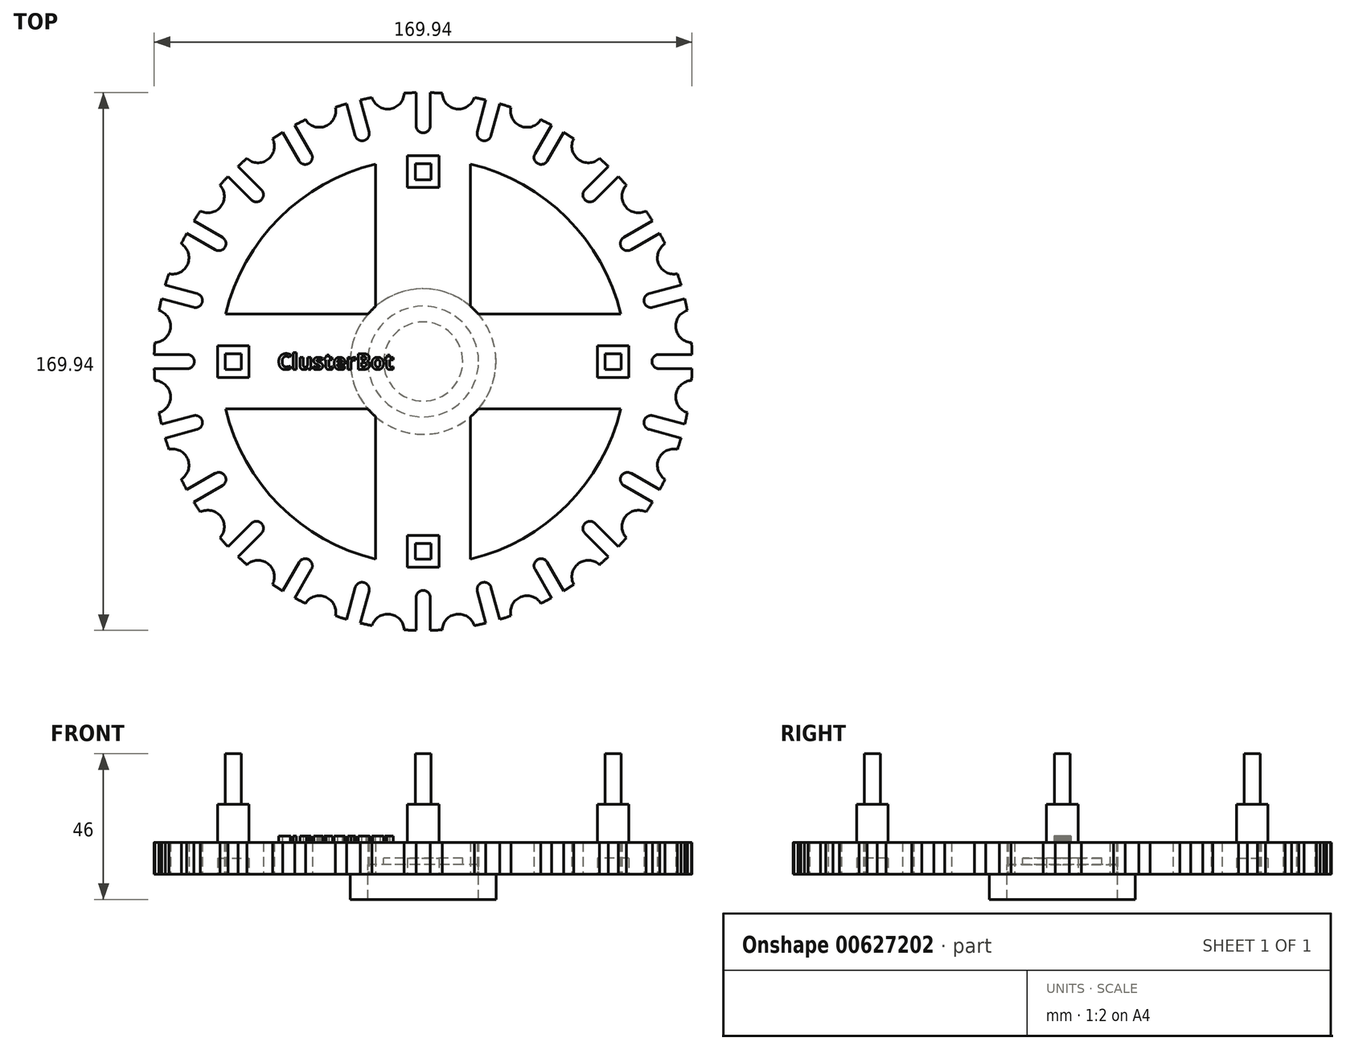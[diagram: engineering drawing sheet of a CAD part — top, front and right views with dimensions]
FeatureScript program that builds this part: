
annotation { "Feature Type Name" : "Feature", "Feature Type Description" : "" }
export const myFeature = defineFeature(function(context is Context, id is Id, definition is map)
    precondition{}
    {
        {
            var Q0;
            Q0=qCreatedBy(makeId("Top.planeOp"),FACE);
            var sketch = newSketch(context, id + "F0", { "sketchPlane" : qUnion([Q0])});
            skCircle(sketch, "E0", {"center": v(0, 0) * mm, "radius": 85 * mm});
            skLineSegment(sketch, "E1", {"start": v(0, 95.93) * mm, "end": v(0, -91) * mm, "construction": true});
            skLineSegment(sketch, "E2", {"start": v(-97.8, 0) * mm, "end": v(95.73, 0) * mm, "construction": true});
            skLineSegment(sketch, "E3", {"start": v(0, 85) * mm, "end": v(2.25, 85) * mm});
            skLineSegment(sketch, "E4", {"start": v(2.25, 85) * mm, "end": v(2.25, 74.54) * mm});
            skLineSegment(sketch, "E5.MirrorCS", {"start": v(0, 85) * mm, "end": v(-2.25, 85) * mm});
            skLineSegment(sketch, "E6.MirrorCS", {"start": v(-2.25, 85) * mm, "end": v(-2.25, 74.54) * mm});
            skArc(sketch, "E7", {"start": v(-2.25, 74.54) * mm, "mid": v(0, 72.3) * mm, "end": v(2.25, 74.54) * mm});
            skLineSegment(sketch, "E8", {"start": v(0, 85) * mm, "end": v(39.95, 85) * mm, "construction": true});
            skCircle(sketch, "E9", {"center": v(11.2, 85) * mm, "radius": 5.2 * mm});
            skLineSegment(sketch, "E10.1.1", {"start": v(-24.17, 81.52) * mm, "end": v(-21.47, 71.42) * mm});
            skLineSegment(sketch, "E10.1.2", {"start": v(-19.83, 82.69) * mm, "end": v(-17.12, 72.59) * mm});
            skArc(sketch, "E10.1.3", {"start": v(-21.47, 71.42) * mm, "mid": v(-18.71, 69.83) * mm, "end": v(-17.12, 72.59) * mm});
            skCircle(sketch, "E10.1.4", {"center": v(-11.2, 85) * mm, "radius": 5.2 * mm});
            skLineSegment(sketch, "E10.2.1", {"start": v(-44.45, 72.49) * mm, "end": v(-39.22, 63.43) * mm});
            skLineSegment(sketch, "E10.2.2", {"start": v(-40.55, 74.74) * mm, "end": v(-35.32, 65.68) * mm});
            skArc(sketch, "E10.2.3", {"start": v(-39.22, 63.43) * mm, "mid": v(-36.15, 62.6) * mm, "end": v(-35.32, 65.68) * mm});
            skCircle(sketch, "E10.2.4", {"center": v(-32.8, 79.2) * mm, "radius": 5.2 * mm});
            skLineSegment(sketch, "E10.3.1", {"start": v(-61.7, 58.51) * mm, "end": v(-54.3, 51.12) * mm});
            skLineSegment(sketch, "E10.3.2", {"start": v(-58.51, 61.7) * mm, "end": v(-51.12, 54.3) * mm});
            skArc(sketch, "E10.3.3", {"start": v(-54.3, 51.12) * mm, "mid": v(-51.12, 51.12) * mm, "end": v(-51.12, 54.3) * mm});
            skCircle(sketch, "E10.3.4", {"center": v(-52.2, 68.02) * mm, "radius": 5.2 * mm});
            skLineSegment(sketch, "E10.4.1", {"start": v(-74.74, 40.55) * mm, "end": v(-65.68, 35.32) * mm});
            skLineSegment(sketch, "E10.4.2", {"start": v(-72.49, 44.45) * mm, "end": v(-63.43, 39.22) * mm});
            skArc(sketch, "E10.4.3", {"start": v(-65.68, 35.32) * mm, "mid": v(-62.6, 36.15) * mm, "end": v(-63.43, 39.22) * mm});
            skCircle(sketch, "E10.4.4", {"center": v(-68.02, 52.2) * mm, "radius": 5.2 * mm});
            skLineSegment(sketch, "E10.5.1", {"start": v(-82.69, 19.83) * mm, "end": v(-72.59, 17.12) * mm});
            skLineSegment(sketch, "E10.5.2", {"start": v(-81.52, 24.17) * mm, "end": v(-71.42, 21.47) * mm});
            skArc(sketch, "E10.5.3", {"start": v(-72.59, 17.12) * mm, "mid": v(-69.83, 18.71) * mm, "end": v(-71.42, 21.47) * mm});
            skCircle(sketch, "E10.5.4", {"center": v(-79.2, 32.8) * mm, "radius": 5.2 * mm});
            skLineSegment(sketch, "E10.6.1", {"start": v(-85, -2.25) * mm, "end": v(-74.54, -2.25) * mm});
            skLineSegment(sketch, "E10.6.2", {"start": v(-85, 2.25) * mm, "end": v(-74.54, 2.25) * mm});
            skArc(sketch, "E10.6.3", {"start": v(-74.54, -2.25) * mm, "mid": v(-72.3, 0) * mm, "end": v(-74.54, 2.25) * mm});
            skCircle(sketch, "E10.6.4", {"center": v(-85, 11.2) * mm, "radius": 5.2 * mm});
            skLineSegment(sketch, "E10.7.1", {"start": v(-81.52, -24.17) * mm, "end": v(-71.42, -21.47) * mm});
            skLineSegment(sketch, "E10.7.2", {"start": v(-82.69, -19.83) * mm, "end": v(-72.59, -17.12) * mm});
            skArc(sketch, "E10.7.3", {"start": v(-71.42, -21.47) * mm, "mid": v(-69.83, -18.71) * mm, "end": v(-72.59, -17.12) * mm});
            skCircle(sketch, "E10.7.4", {"center": v(-85, -11.2) * mm, "radius": 5.2 * mm});
            skLineSegment(sketch, "E10.8.1", {"start": v(-72.49, -44.45) * mm, "end": v(-63.43, -39.22) * mm});
            skLineSegment(sketch, "E10.8.2", {"start": v(-74.74, -40.55) * mm, "end": v(-65.68, -35.32) * mm});
            skArc(sketch, "E10.8.3", {"start": v(-63.43, -39.22) * mm, "mid": v(-62.6, -36.15) * mm, "end": v(-65.68, -35.32) * mm});
            skCircle(sketch, "E10.8.4", {"center": v(-79.2, -32.8) * mm, "radius": 5.2 * mm});
            skLineSegment(sketch, "E10.9.1", {"start": v(-58.51, -61.7) * mm, "end": v(-51.12, -54.3) * mm});
            skLineSegment(sketch, "E10.9.2", {"start": v(-61.7, -58.51) * mm, "end": v(-54.3, -51.12) * mm});
            skArc(sketch, "E10.9.3", {"start": v(-51.12, -54.3) * mm, "mid": v(-51.12, -51.12) * mm, "end": v(-54.3, -51.12) * mm});
            skCircle(sketch, "E10.9.4", {"center": v(-68.02, -52.2) * mm, "radius": 5.2 * mm});
            skLineSegment(sketch, "E10.10.1", {"start": v(-40.55, -74.74) * mm, "end": v(-35.32, -65.68) * mm});
            skLineSegment(sketch, "E10.10.2", {"start": v(-44.45, -72.49) * mm, "end": v(-39.22, -63.43) * mm});
            skArc(sketch, "E10.10.3", {"start": v(-35.32, -65.68) * mm, "mid": v(-36.15, -62.6) * mm, "end": v(-39.22, -63.43) * mm});
            skCircle(sketch, "E10.10.4", {"center": v(-52.2, -68.02) * mm, "radius": 5.2 * mm});
            skLineSegment(sketch, "E10.11.1", {"start": v(-19.83, -82.69) * mm, "end": v(-17.12, -72.59) * mm});
            skLineSegment(sketch, "E10.11.2", {"start": v(-24.17, -81.52) * mm, "end": v(-21.47, -71.42) * mm});
            skArc(sketch, "E10.11.3", {"start": v(-17.12, -72.59) * mm, "mid": v(-18.71, -69.83) * mm, "end": v(-21.47, -71.42) * mm});
            skCircle(sketch, "E10.11.4", {"center": v(-32.8, -79.2) * mm, "radius": 5.2 * mm});
            skLineSegment(sketch, "E10.12.1", {"start": v(2.25, -85) * mm, "end": v(2.25, -74.54) * mm});
            skLineSegment(sketch, "E10.12.2", {"start": v(-2.25, -85) * mm, "end": v(-2.25, -74.54) * mm});
            skArc(sketch, "E10.12.3", {"start": v(2.25, -74.54) * mm, "mid": v(0, -72.3) * mm, "end": v(-2.25, -74.54) * mm});
            skCircle(sketch, "E10.12.4", {"center": v(-11.2, -85) * mm, "radius": 5.2 * mm});
            skLineSegment(sketch, "E10.13.1", {"start": v(24.17, -81.52) * mm, "end": v(21.47, -71.42) * mm});
            skLineSegment(sketch, "E10.13.2", {"start": v(19.83, -82.69) * mm, "end": v(17.12, -72.59) * mm});
            skArc(sketch, "E10.13.3", {"start": v(21.47, -71.42) * mm, "mid": v(18.71, -69.83) * mm, "end": v(17.12, -72.59) * mm});
            skCircle(sketch, "E10.13.4", {"center": v(11.2, -85) * mm, "radius": 5.2 * mm});
            skLineSegment(sketch, "E10.14.1", {"start": v(44.45, -72.49) * mm, "end": v(39.22, -63.43) * mm});
            skLineSegment(sketch, "E10.14.2", {"start": v(40.55, -74.74) * mm, "end": v(35.32, -65.68) * mm});
            skArc(sketch, "E10.14.3", {"start": v(39.22, -63.43) * mm, "mid": v(36.15, -62.6) * mm, "end": v(35.32, -65.68) * mm});
            skCircle(sketch, "E10.14.4", {"center": v(32.8, -79.2) * mm, "radius": 5.2 * mm});
            skLineSegment(sketch, "E11.bottom", {"start": v(2.5, 57.5) * mm, "end": v(-2.5, 57.5) * mm});
            skLineSegment(sketch, "E11.top", {"start": v(2.5, 62.5) * mm, "end": v(-2.5, 62.5) * mm});
            skLineSegment(sketch, "E11.left", {"start": v(2.5, 57.5) * mm, "end": v(2.5, 62.5) * mm});
            skLineSegment(sketch, "E11.right", {"start": v(-2.5, 57.5) * mm, "end": v(-2.5, 62.5) * mm});
            skPoint(sketch, "E11.middle", {"position": v(0, 60) * mm});
            skLineSegment(sketch, "E12.MirrorCS", {"start": v(2.5, -57.5) * mm, "end": v(-2.5, -57.5) * mm});
            skLineSegment(sketch, "E13.MirrorCS", {"start": v(2.5, -57.5) * mm, "end": v(2.5, -62.5) * mm});
            skLineSegment(sketch, "E14.MirrorCS", {"start": v(2.5, -62.5) * mm, "end": v(-2.5, -62.5) * mm});
            skLineSegment(sketch, "E15.MirrorCS", {"start": v(-2.5, -57.5) * mm, "end": v(-2.5, -62.5) * mm});
            skLineSegment(sketch, "E16.bottom", {"start": v(57.5, 2.5) * mm, "end": v(62.5, 2.5) * mm});
            skLineSegment(sketch, "E16.top", {"start": v(57.5, -2.5) * mm, "end": v(62.5, -2.5) * mm});
            skLineSegment(sketch, "E16.left", {"start": v(57.5, 2.5) * mm, "end": v(57.5, -2.5) * mm});
            skLineSegment(sketch, "E16.right", {"start": v(62.5, 2.5) * mm, "end": v(62.5, -2.5) * mm});
            skPoint(sketch, "E16.middle", {"position": v(60, 0) * mm});
            skLineSegment(sketch, "E17.MirrorCS", {"start": v(-57.5, 2.5) * mm, "end": v(-62.5, 2.5) * mm});
            skLineSegment(sketch, "E18.MirrorCS", {"start": v(-62.5, 2.5) * mm, "end": v(-62.5, -2.5) * mm});
            skLineSegment(sketch, "E19.MirrorCS", {"start": v(-57.5, -2.5) * mm, "end": v(-62.5, -2.5) * mm});
            skLineSegment(sketch, "E20.MirrorCS", {"start": v(-57.5, 2.5) * mm, "end": v(-57.5, -2.5) * mm});
            skLineSegment(sketch, "E21.bottom", {"start": v(5, 55) * mm, "end": v(-5, 55) * mm});
            skLineSegment(sketch, "E21.top", {"start": v(5, 65) * mm, "end": v(-5, 65) * mm});
            skLineSegment(sketch, "E21.left", {"start": v(5, 55) * mm, "end": v(5, 65) * mm});
            skLineSegment(sketch, "E21.right", {"start": v(-5, 55) * mm, "end": v(-5, 65) * mm});
            skLineSegment(sketch, "E22.bottom", {"start": v(65, -5) * mm, "end": v(55, -5) * mm});
            skLineSegment(sketch, "E22.top", {"start": v(65, 5) * mm, "end": v(55, 5) * mm});
            skLineSegment(sketch, "E22.left", {"start": v(65, -5) * mm, "end": v(65, 5) * mm});
            skLineSegment(sketch, "E22.right", {"start": v(55, -5) * mm, "end": v(55, 5) * mm});
            skLineSegment(sketch, "E23.MirrorCS", {"start": v(-65, 5) * mm, "end": v(-55, 5) * mm});
            skLineSegment(sketch, "E24.MirrorCS", {"start": v(-65, -5) * mm, "end": v(-65, 5) * mm});
            skLineSegment(sketch, "E25.MirrorCS", {"start": v(-55, -5) * mm, "end": v(-55, 5) * mm});
            skLineSegment(sketch, "E26.MirrorCS", {"start": v(-65, -5) * mm, "end": v(-55, -5) * mm});
            skLineSegment(sketch, "E27.MirrorCS", {"start": v(-5, -55) * mm, "end": v(-5, -65) * mm});
            skLineSegment(sketch, "E28.MirrorCS", {"start": v(5, -65) * mm, "end": v(-5, -65) * mm});
            skLineSegment(sketch, "E29.MirrorCS", {"start": v(5, -55) * mm, "end": v(5, -65) * mm});
            skLineSegment(sketch, "E30.MirrorCS", {"start": v(5, -55) * mm, "end": v(-5, -55) * mm});
            skCircle(sketch, "E31", {"center": v(0, 0) * mm, "radius": 12.5 * mm});
            skCircle(sketch, "E32", {"center": v(0, 0) * mm, "radius": 17.5 * mm});
            skCircle(sketch, "E33", {"center": v(0, 0) * mm, "radius": 23 * mm});
            skLineSegment(sketch, "E34", {"start": v(-15, 17.1) * mm, "end": v(-15, -32.9) * mm, "construction": true});
            skLineSegment(sketch, "E35", {"start": v(-116.33, 15) * mm, "end": v(-66.33, 15) * mm, "construction": true});
            skLineSegment(sketch, "E36", {"start": v(-15, 15) * mm, "end": v(0, 0) * mm, "construction": true});
            skLineSegment(sketch, "E37", {"start": v(-17.44, 15) * mm, "end": v(-62.44, 15) * mm});
            skLineSegment(sketch, "E38", {"start": v(-15, 17.44) * mm, "end": v(-15, 62.44) * mm});
            skLineSegment(sketch, "E39", {"start": v(0, 0) * mm, "end": v(-15, 62.44) * mm, "construction": true});
            skArc(sketch, "E40", {"start": v(-15, 62.44) * mm, "mid": v(-45.4, 45.4) * mm, "end": v(-62.44, 15) * mm});
            skLineSegment(sketch, "E41.MirrorCS", {"start": v(17.44, 15) * mm, "end": v(62.44, 15) * mm});
            skLineSegment(sketch, "E42.MirrorCS", {"start": v(15, 17.44) * mm, "end": v(15, 62.44) * mm});
            skArc(sketch, "E43.MirrorCS", {"start": v(15, 62.44) * mm, "mid": v(45.4, 45.4) * mm, "end": v(62.44, 15) * mm});
            skLineSegment(sketch, "E44.MirrorCS", {"start": v(-17.44, -15) * mm, "end": v(-62.44, -15) * mm});
            skArc(sketch, "E45.MirrorCS", {"start": v(-15, -62.44) * mm, "mid": v(-45.4, -45.4) * mm, "end": v(-62.44, -15) * mm});
            skLineSegment(sketch, "E46.MirrorCS", {"start": v(-15, -17.44) * mm, "end": v(-15, -62.44) * mm});
            skLineSegment(sketch, "E47.MirrorCS", {"start": v(15, -17.44) * mm, "end": v(15, -62.44) * mm});
            skArc(sketch, "E48.MirrorCS", {"start": v(15, -62.44) * mm, "mid": v(45.4, -45.4) * mm, "end": v(62.44, -15) * mm});
            skLineSegment(sketch, "E49.MirrorCS", {"start": v(17.44, -15) * mm, "end": v(62.44, -15) * mm});
            skLineSegment(sketch, "E50", {"start": v(-5, -65) * mm, "end": v(-9, -65) * mm});
            skLineSegment(sketch, "E51.MirrorCS", {"start": v(5, -65) * mm, "end": v(9, -65) * mm});
            skLineSegment(sketch, "E52.MirrorCS", {"start": v(-5, 65) * mm, "end": v(-9, 65) * mm});
            skLineSegment(sketch, "E53.MirrorCS", {"start": v(5, 65) * mm, "end": v(9, 65) * mm});
            skLineSegment(sketch, "E54", {"start": v(-65, -5) * mm, "end": v(-65, -9) * mm});
            skLineSegment(sketch, "E55.MirrorCS", {"start": v(-65, 5) * mm, "end": v(-65, 9) * mm});
            skLineSegment(sketch, "E56.MirrorCS", {"start": v(65, -5) * mm, "end": v(65, -9) * mm});
            skLineSegment(sketch, "E57.MirrorCS", {"start": v(65, 5) * mm, "end": v(65, 9) * mm});
            skLineSegment(sketch, "E58", {"start": v(55, -5) * mm, "end": v(22.45, -5) * mm});
            skLineSegment(sketch, "E59", {"start": v(65, -9) * mm, "end": v(21.17, -9) * mm});
            skLineSegment(sketch, "E60.MirrorCS", {"start": v(55, 5) * mm, "end": v(22.45, 5) * mm});
            skLineSegment(sketch, "E61.MirrorCS", {"start": v(65, 9) * mm, "end": v(21.17, 9) * mm});
            skLineSegment(sketch, "E62.MirrorCS", {"start": v(-65, -9) * mm, "end": v(-21.17, -9) * mm});
            skLineSegment(sketch, "E63.MirrorCS", {"start": v(-55, -5) * mm, "end": v(-22.45, -5) * mm});
            skLineSegment(sketch, "E64.MirrorCS", {"start": v(-55, 5) * mm, "end": v(-22.45, 5) * mm});
            skLineSegment(sketch, "E65.MirrorCS", {"start": v(-65, 9) * mm, "end": v(-21.17, 9) * mm});
            skLineSegment(sketch, "E66", {"start": v(-5, -55) * mm, "end": v(-5, -22.45) * mm});
            skLineSegment(sketch, "E67", {"start": v(5, -55) * mm, "end": v(5, -22.45) * mm});
            skLineSegment(sketch, "E68", {"start": v(-9, -65) * mm, "end": v(-9, -21.17) * mm});
            skLineSegment(sketch, "E69", {"start": v(9, -65) * mm, "end": v(9, -21.17) * mm});
            skLineSegment(sketch, "E70.MirrorCS", {"start": v(-9, 65) * mm, "end": v(-9, 21.17) * mm});
            skLineSegment(sketch, "E71.MirrorCS", {"start": v(-5, 55) * mm, "end": v(-5, 22.45) * mm});
            skLineSegment(sketch, "E72.MirrorCS", {"start": v(5, 55) * mm, "end": v(5, 22.45) * mm});
            skLineSegment(sketch, "E73.MirrorCS", {"start": v(9, 65) * mm, "end": v(9, 21.17) * mm});
            skLineSegment(sketch, "E74.2.15.0", {"start": v(61.7, -58.51) * mm, "end": v(54.3, -51.12) * mm});
            skLineSegment(sketch, "E74.5.15.0", {"start": v(58.51, -61.7) * mm, "end": v(51.12, -54.3) * mm});
            skArc(sketch, "E74.8.15.0", {"start": v(54.3, -51.12) * mm, "mid": v(51.12, -51.12) * mm, "end": v(51.12, -54.3) * mm});
            skCircle(sketch, "E74.12.15.0", {"center": v(52.2, -68.02) * mm, "radius": 5.2 * mm});
            skLineSegment(sketch, "E74.2.16.0", {"start": v(74.74, -40.55) * mm, "end": v(65.68, -35.32) * mm});
            skLineSegment(sketch, "E74.5.16.0", {"start": v(72.49, -44.45) * mm, "end": v(63.43, -39.22) * mm});
            skArc(sketch, "E74.8.16.0", {"start": v(65.68, -35.32) * mm, "mid": v(62.6, -36.15) * mm, "end": v(63.43, -39.22) * mm});
            skCircle(sketch, "E74.12.16.0", {"center": v(68.02, -52.2) * mm, "radius": 5.2 * mm});
            skLineSegment(sketch, "E74.2.17.0", {"start": v(82.69, -19.83) * mm, "end": v(72.59, -17.12) * mm});
            skLineSegment(sketch, "E74.5.17.0", {"start": v(81.52, -24.17) * mm, "end": v(71.42, -21.47) * mm});
            skArc(sketch, "E74.8.17.0", {"start": v(72.59, -17.12) * mm, "mid": v(69.83, -18.71) * mm, "end": v(71.42, -21.47) * mm});
            skCircle(sketch, "E74.12.17.0", {"center": v(79.2, -32.8) * mm, "radius": 5.2 * mm});
            skLineSegment(sketch, "E74.2.18.0", {"start": v(85, 2.25) * mm, "end": v(74.54, 2.25) * mm});
            skLineSegment(sketch, "E74.5.18.0", {"start": v(85, -2.25) * mm, "end": v(74.54, -2.25) * mm});
            skArc(sketch, "E74.8.18.0", {"start": v(74.54, 2.25) * mm, "mid": v(72.3, 0) * mm, "end": v(74.54, -2.25) * mm});
            skCircle(sketch, "E74.12.18.0", {"center": v(85, -11.2) * mm, "radius": 5.2 * mm});
            skLineSegment(sketch, "E74.2.19.0", {"start": v(81.52, 24.17) * mm, "end": v(71.42, 21.47) * mm});
            skArc(sketch, "E74.8.19.0", {"start": v(71.42, 21.47) * mm, "mid": v(69.83, 18.71) * mm, "end": v(72.59, 17.12) * mm});
            skCircle(sketch, "E74.12.19.0", {"center": v(85, 11.2) * mm, "radius": 5.2 * mm});
            skLineSegment(sketch, "E74.2.20.0", {"start": v(72.49, 44.45) * mm, "end": v(63.43, 39.22) * mm});
            skLineSegment(sketch, "E74.5.20.0", {"start": v(74.74, 40.55) * mm, "end": v(65.68, 35.32) * mm});
            skArc(sketch, "E74.8.20.0", {"start": v(63.43, 39.22) * mm, "mid": v(62.6, 36.15) * mm, "end": v(65.68, 35.32) * mm});
            skCircle(sketch, "E74.12.20.0", {"center": v(79.2, 32.8) * mm, "radius": 5.2 * mm});
            skLineSegment(sketch, "E74.2.21.0", {"start": v(58.51, 61.7) * mm, "end": v(51.12, 54.3) * mm});
            skLineSegment(sketch, "E74.5.21.0", {"start": v(61.7, 58.51) * mm, "end": v(54.3, 51.12) * mm});
            skArc(sketch, "E74.8.21.0", {"start": v(51.12, 54.3) * mm, "mid": v(51.12, 51.12) * mm, "end": v(54.3, 51.12) * mm});
            skCircle(sketch, "E74.12.21.0", {"center": v(68.02, 52.2) * mm, "radius": 5.2 * mm});
            skLineSegment(sketch, "E74.2.22.0", {"start": v(40.55, 74.74) * mm, "end": v(35.32, 65.68) * mm});
            skLineSegment(sketch, "E74.5.22.0", {"start": v(44.45, 72.49) * mm, "end": v(39.22, 63.43) * mm});
            skArc(sketch, "E74.8.22.0", {"start": v(35.32, 65.68) * mm, "mid": v(36.15, 62.6) * mm, "end": v(39.22, 63.43) * mm});
            skCircle(sketch, "E74.12.22.0", {"center": v(52.2, 68.02) * mm, "radius": 5.2 * mm});
            skLineSegment(sketch, "E74.2.23.0", {"start": v(19.83, 82.69) * mm, "end": v(17.12, 72.59) * mm});
            skLineSegment(sketch, "E74.5.23.0", {"start": v(24.17, 81.52) * mm, "end": v(21.47, 71.42) * mm});
            skArc(sketch, "E74.8.23.0", {"start": v(17.12, 72.59) * mm, "mid": v(18.71, 69.83) * mm, "end": v(21.47, 71.42) * mm});
            skCircle(sketch, "E74.12.23.0", {"center": v(32.8, 79.2) * mm, "radius": 5.2 * mm});
            skLineSegment(sketch, "E75", {"start": v(120, 11.77) * mm, "end": v(120, -18.04) * mm, "construction": true});
            skCircle(sketch, "E76.MirrorC", {"center": v(240, 0) * mm, "radius": 17.5 * mm});
            skCircle(sketch, "E77.MirrorC", {"center": v(240, 0) * mm, "radius": 12.5 * mm});
            skCircle(sketch, "E78.MirrorC", {"center": v(240, 0) * mm, "radius": 23 * mm});
            skLineSegment(sketch, "E79", {"start": v(72.59, 17.12) * mm, "end": v(82.66, 19.82) * mm});
            skCircle(sketch, "E80", {"center": v(240, 0) * mm, "radius": 75 * mm});
            skLineSegment(sketch, "E81", {"start": v(240, 0) * mm, "end": v(240, 75.65) * mm, "construction": true});
            skCircle(sketch, "E82", {"center": v(240, 75.65) * mm, "radius": 3.87 * mm});
            skLineSegment(sketch, "E83", {"start": v(240, 75.65) * mm, "end": v(249.79, 74.36) * mm});
            skLineSegment(sketch, "E84", {"start": v(240, 0) * mm, "end": v(249.79, 74.36) * mm, "construction": true});
            skLineSegment(sketch, "E85", {"start": v(249.79, 74.36) * mm, "end": v(251.82, 74.1) * mm});
            skLineSegment(sketch, "E86", {"start": v(251.82, 74.1) * mm, "end": v(247.76, 74.63) * mm});
            skCircle(sketch, "E87", {"center": v(248.59, 65.21) * mm, "radius": 2.05 * mm});
            skLineSegment(sketch, "E88", {"start": v(247.76, 74.63) * mm, "end": v(246.55, 65.48) * mm});
            skLineSegment(sketch, "E89.MirrorCS", {"start": v(251.82, 74.1) * mm, "end": v(250.62, 64.94) * mm});
            skLineSegment(sketch, "E90.1.0", {"start": v(228.18, 74.1) * mm, "end": v(229.38, 64.94) * mm});
            skLineSegment(sketch, "E90.1.1", {"start": v(220.42, 73.07) * mm, "end": v(230.21, 74.36) * mm});
            skLineSegment(sketch, "E90.1.2", {"start": v(232.24, 74.63) * mm, "end": v(233.45, 65.48) * mm});
            skCircle(sketch, "E90.1.3", {"center": v(231.41, 65.21) * mm, "radius": 2.05 * mm});
            skLineSegment(sketch, "E90.1.4", {"start": v(232.24, 74.63) * mm, "end": v(228.18, 74.1) * mm});
            skCircle(sketch, "E90.1.5", {"center": v(220.42, 73.07) * mm, "radius": 3.87 * mm});
            skLineSegment(sketch, "E90.1.6", {"start": v(230.21, 74.36) * mm, "end": v(232.24, 74.63) * mm});
            skLineSegment(sketch, "E90.2.0", {"start": v(209.4, 68.5) * mm, "end": v(212.94, 59.98) * mm});
            skLineSegment(sketch, "E90.2.1", {"start": v(202.18, 65.51) * mm, "end": v(211.3, 69.3) * mm});
            skLineSegment(sketch, "E90.2.2", {"start": v(213.2, 70.08) * mm, "end": v(216.72, 61.55) * mm});
            skCircle(sketch, "E90.2.3", {"center": v(214.83, 60.77) * mm, "radius": 2.05 * mm});
            skLineSegment(sketch, "E90.2.4", {"start": v(213.2, 70.08) * mm, "end": v(209.4, 68.5) * mm});
            skCircle(sketch, "E90.2.5", {"center": v(202.18, 65.51) * mm, "radius": 3.87 * mm});
            skLineSegment(sketch, "E90.2.6", {"start": v(211.3, 69.3) * mm, "end": v(213.2, 70.08) * mm});
            skLineSegment(sketch, "E90.3.0", {"start": v(192.72, 58.25) * mm, "end": v(198.33, 50.93) * mm});
            skLineSegment(sketch, "E90.3.1", {"start": v(186.5, 53.5) * mm, "end": v(194.34, 59.5) * mm});
            skLineSegment(sketch, "E90.3.2", {"start": v(195.97, 60.75) * mm, "end": v(201.59, 53.43) * mm});
            skCircle(sketch, "E90.3.3", {"center": v(199.96, 52.18) * mm, "radius": 2.05 * mm});
            skLineSegment(sketch, "E90.3.4", {"start": v(195.97, 60.75) * mm, "end": v(192.72, 58.25) * mm});
            skCircle(sketch, "E90.3.5", {"center": v(186.5, 53.5) * mm, "radius": 3.87 * mm});
            skLineSegment(sketch, "E90.3.6", {"start": v(194.34, 59.5) * mm, "end": v(195.97, 60.75) * mm});
            skLineSegment(sketch, "E90.4.0", {"start": v(179.25, 44.03) * mm, "end": v(186.57, 38.41) * mm});
            skLineSegment(sketch, "E90.4.1", {"start": v(174.49, 37.82) * mm, "end": v(180.5, 45.66) * mm});
            skLineSegment(sketch, "E90.4.2", {"start": v(181.75, 47.28) * mm, "end": v(189.07, 41.67) * mm});
            skCircle(sketch, "E90.4.3", {"center": v(187.82, 40.04) * mm, "radius": 2.05 * mm});
            skLineSegment(sketch, "E90.4.4", {"start": v(181.75, 47.28) * mm, "end": v(179.25, 44.03) * mm});
            skCircle(sketch, "E90.4.5", {"center": v(174.49, 37.82) * mm, "radius": 3.87 * mm});
            skLineSegment(sketch, "E90.4.6", {"start": v(180.5, 45.66) * mm, "end": v(181.75, 47.28) * mm});
            skLineSegment(sketch, "E90.5.0", {"start": v(169.92, 26.8) * mm, "end": v(178.45, 23.28) * mm});
            skLineSegment(sketch, "E90.5.1", {"start": v(166.93, 19.58) * mm, "end": v(170.7, 28.7) * mm});
            skLineSegment(sketch, "E90.5.2", {"start": v(171.5, 30.6) * mm, "end": v(180.02, 27.06) * mm});
            skCircle(sketch, "E90.5.3", {"center": v(179.23, 25.17) * mm, "radius": 2.05 * mm});
            skLineSegment(sketch, "E90.5.4", {"start": v(171.5, 30.6) * mm, "end": v(169.92, 26.8) * mm});
            skCircle(sketch, "E90.5.5", {"center": v(166.93, 19.58) * mm, "radius": 3.87 * mm});
            skLineSegment(sketch, "E90.5.6", {"start": v(170.7, 28.7) * mm, "end": v(171.5, 30.6) * mm});
            skLineSegment(sketch, "E90.6.0", {"start": v(165.37, 7.76) * mm, "end": v(174.52, 6.55) * mm});
            skLineSegment(sketch, "E90.6.1", {"start": v(164.35, 0) * mm, "end": v(165.64, 9.79) * mm});
            skLineSegment(sketch, "E90.6.2", {"start": v(165.9, 11.82) * mm, "end": v(175.06, 10.62) * mm});
            skCircle(sketch, "E90.6.3", {"center": v(174.79, 8.59) * mm, "radius": 2.05 * mm});
            skLineSegment(sketch, "E90.6.4", {"start": v(165.9, 11.82) * mm, "end": v(165.37, 7.76) * mm});
            skCircle(sketch, "E90.6.5", {"center": v(164.35, 0) * mm, "radius": 3.87 * mm});
            skLineSegment(sketch, "E90.6.6", {"start": v(165.64, 9.79) * mm, "end": v(165.9, 11.82) * mm});
            skLineSegment(sketch, "E90.7.0", {"start": v(165.9, -11.82) * mm, "end": v(175.06, -10.62) * mm});
            skLineSegment(sketch, "E90.7.1", {"start": v(166.93, -19.58) * mm, "end": v(165.64, -9.79) * mm});
            skLineSegment(sketch, "E90.7.2", {"start": v(165.37, -7.76) * mm, "end": v(174.52, -6.55) * mm});
            skCircle(sketch, "E90.7.3", {"center": v(174.79, -8.59) * mm, "radius": 2.05 * mm});
            skLineSegment(sketch, "E90.7.4", {"start": v(165.37, -7.76) * mm, "end": v(165.9, -11.82) * mm});
            skCircle(sketch, "E90.7.5", {"center": v(166.93, -19.58) * mm, "radius": 3.87 * mm});
            skLineSegment(sketch, "E90.7.6", {"start": v(165.64, -9.79) * mm, "end": v(165.37, -7.76) * mm});
            skLineSegment(sketch, "E90.8.0", {"start": v(171.5, -30.6) * mm, "end": v(180.02, -27.06) * mm});
            skLineSegment(sketch, "E90.8.1", {"start": v(174.49, -37.82) * mm, "end": v(170.7, -28.7) * mm});
            skLineSegment(sketch, "E90.8.2", {"start": v(169.92, -26.8) * mm, "end": v(178.45, -23.28) * mm});
            skCircle(sketch, "E90.8.3", {"center": v(179.23, -25.17) * mm, "radius": 2.05 * mm});
            skLineSegment(sketch, "E90.8.4", {"start": v(169.92, -26.8) * mm, "end": v(171.5, -30.6) * mm});
            skCircle(sketch, "E90.8.5", {"center": v(174.49, -37.82) * mm, "radius": 3.87 * mm});
            skLineSegment(sketch, "E90.8.6", {"start": v(170.7, -28.7) * mm, "end": v(169.92, -26.8) * mm});
            skLineSegment(sketch, "E90.9.0", {"start": v(181.75, -47.28) * mm, "end": v(189.07, -41.67) * mm});
            skLineSegment(sketch, "E90.9.1", {"start": v(186.5, -53.5) * mm, "end": v(180.5, -45.66) * mm});
            skLineSegment(sketch, "E90.9.2", {"start": v(179.25, -44.03) * mm, "end": v(186.57, -38.41) * mm});
            skCircle(sketch, "E90.9.3", {"center": v(187.82, -40.04) * mm, "radius": 2.05 * mm});
            skLineSegment(sketch, "E90.9.4", {"start": v(179.25, -44.03) * mm, "end": v(181.75, -47.28) * mm});
            skCircle(sketch, "E90.9.5", {"center": v(186.5, -53.5) * mm, "radius": 3.87 * mm});
            skLineSegment(sketch, "E90.9.6", {"start": v(180.5, -45.66) * mm, "end": v(179.25, -44.03) * mm});
            skLineSegment(sketch, "E90.10.0", {"start": v(195.97, -60.75) * mm, "end": v(201.59, -53.43) * mm});
            skLineSegment(sketch, "E90.10.1", {"start": v(202.18, -65.51) * mm, "end": v(194.34, -59.5) * mm});
            skLineSegment(sketch, "E90.10.2", {"start": v(192.72, -58.25) * mm, "end": v(198.33, -50.93) * mm});
            skCircle(sketch, "E90.10.3", {"center": v(199.96, -52.18) * mm, "radius": 2.05 * mm});
            skLineSegment(sketch, "E90.10.4", {"start": v(192.72, -58.25) * mm, "end": v(195.97, -60.75) * mm});
            skCircle(sketch, "E90.10.5", {"center": v(202.18, -65.51) * mm, "radius": 3.87 * mm});
            skLineSegment(sketch, "E90.10.6", {"start": v(194.34, -59.5) * mm, "end": v(192.72, -58.25) * mm});
            skLineSegment(sketch, "E90.11.0", {"start": v(213.2, -70.08) * mm, "end": v(216.72, -61.55) * mm});
            skLineSegment(sketch, "E90.11.1", {"start": v(220.42, -73.07) * mm, "end": v(211.3, -69.3) * mm});
            skLineSegment(sketch, "E90.11.2", {"start": v(209.4, -68.5) * mm, "end": v(212.94, -59.98) * mm});
            skCircle(sketch, "E90.11.3", {"center": v(214.83, -60.77) * mm, "radius": 2.05 * mm});
            skLineSegment(sketch, "E90.11.4", {"start": v(209.4, -68.5) * mm, "end": v(213.2, -70.08) * mm});
            skCircle(sketch, "E90.11.5", {"center": v(220.42, -73.07) * mm, "radius": 3.87 * mm});
            skLineSegment(sketch, "E90.11.6", {"start": v(211.3, -69.3) * mm, "end": v(209.4, -68.5) * mm});
            skLineSegment(sketch, "E90.12.0", {"start": v(232.24, -74.63) * mm, "end": v(233.45, -65.48) * mm});
            skLineSegment(sketch, "E90.12.1", {"start": v(240, -75.65) * mm, "end": v(230.21, -74.36) * mm});
            skLineSegment(sketch, "E90.12.2", {"start": v(228.18, -74.1) * mm, "end": v(229.38, -64.94) * mm});
            skCircle(sketch, "E90.12.3", {"center": v(231.41, -65.21) * mm, "radius": 2.05 * mm});
            skLineSegment(sketch, "E90.12.4", {"start": v(228.18, -74.1) * mm, "end": v(232.24, -74.63) * mm});
            skCircle(sketch, "E90.12.5", {"center": v(240, -75.65) * mm, "radius": 3.87 * mm});
            skLineSegment(sketch, "E90.12.6", {"start": v(230.21, -74.36) * mm, "end": v(228.18, -74.1) * mm});
            skLineSegment(sketch, "E90.13.0", {"start": v(251.82, -74.1) * mm, "end": v(250.62, -64.94) * mm});
            skLineSegment(sketch, "E90.13.1", {"start": v(259.58, -73.07) * mm, "end": v(249.79, -74.36) * mm});
            skLineSegment(sketch, "E90.13.2", {"start": v(247.76, -74.63) * mm, "end": v(246.55, -65.48) * mm});
            skCircle(sketch, "E90.13.3", {"center": v(248.59, -65.21) * mm, "radius": 2.05 * mm});
            skLineSegment(sketch, "E90.13.4", {"start": v(247.76, -74.63) * mm, "end": v(251.82, -74.1) * mm});
            skCircle(sketch, "E90.13.5", {"center": v(259.58, -73.07) * mm, "radius": 3.87 * mm});
            skLineSegment(sketch, "E90.13.6", {"start": v(249.79, -74.36) * mm, "end": v(247.76, -74.63) * mm});
            skLineSegment(sketch, "E90.14.0", {"start": v(270.6, -68.5) * mm, "end": v(267.06, -59.98) * mm});
            skLineSegment(sketch, "E90.14.1", {"start": v(277.82, -65.51) * mm, "end": v(268.7, -69.3) * mm});
            skLineSegment(sketch, "E90.14.2", {"start": v(266.8, -70.08) * mm, "end": v(263.28, -61.55) * mm});
            skCircle(sketch, "E90.14.3", {"center": v(265.17, -60.77) * mm, "radius": 2.05 * mm});
            skLineSegment(sketch, "E90.14.4", {"start": v(266.8, -70.08) * mm, "end": v(270.6, -68.5) * mm});
            skCircle(sketch, "E90.14.5", {"center": v(277.82, -65.51) * mm, "radius": 3.87 * mm});
            skLineSegment(sketch, "E90.14.6", {"start": v(268.7, -69.3) * mm, "end": v(266.8, -70.08) * mm});
            skLineSegment(sketch, "E90.15.0", {"start": v(287.28, -58.25) * mm, "end": v(281.67, -50.93) * mm});
            skLineSegment(sketch, "E90.15.1", {"start": v(293.5, -53.5) * mm, "end": v(285.66, -59.5) * mm});
            skLineSegment(sketch, "E90.15.2", {"start": v(284.03, -60.75) * mm, "end": v(278.41, -53.43) * mm});
            skCircle(sketch, "E90.15.3", {"center": v(280.04, -52.18) * mm, "radius": 2.05 * mm});
            skLineSegment(sketch, "E90.15.4", {"start": v(284.03, -60.75) * mm, "end": v(287.28, -58.25) * mm});
            skCircle(sketch, "E90.15.5", {"center": v(293.5, -53.5) * mm, "radius": 3.87 * mm});
            skLineSegment(sketch, "E90.15.6", {"start": v(285.66, -59.5) * mm, "end": v(284.03, -60.75) * mm});
            skLineSegment(sketch, "E90.16.0", {"start": v(300.75, -44.03) * mm, "end": v(293.43, -38.41) * mm});
            skLineSegment(sketch, "E90.16.1", {"start": v(305.51, -37.82) * mm, "end": v(299.5, -45.66) * mm});
            skLineSegment(sketch, "E90.16.2", {"start": v(298.25, -47.28) * mm, "end": v(290.93, -41.67) * mm});
            skCircle(sketch, "E90.16.3", {"center": v(292.18, -40.04) * mm, "radius": 2.05 * mm});
            skLineSegment(sketch, "E90.16.4", {"start": v(298.25, -47.28) * mm, "end": v(300.75, -44.03) * mm});
            skCircle(sketch, "E90.16.5", {"center": v(305.51, -37.82) * mm, "radius": 3.87 * mm});
            skLineSegment(sketch, "E90.16.6", {"start": v(299.5, -45.66) * mm, "end": v(298.25, -47.28) * mm});
            skLineSegment(sketch, "E90.17.0", {"start": v(310.08, -26.8) * mm, "end": v(301.55, -23.28) * mm});
            skLineSegment(sketch, "E90.17.1", {"start": v(313.07, -19.58) * mm, "end": v(309.3, -28.7) * mm});
            skLineSegment(sketch, "E90.17.2", {"start": v(308.5, -30.6) * mm, "end": v(299.98, -27.06) * mm});
            skCircle(sketch, "E90.17.3", {"center": v(300.77, -25.17) * mm, "radius": 2.05 * mm});
            skLineSegment(sketch, "E90.17.4", {"start": v(308.5, -30.6) * mm, "end": v(310.08, -26.8) * mm});
            skCircle(sketch, "E90.17.5", {"center": v(313.07, -19.58) * mm, "radius": 3.87 * mm});
            skLineSegment(sketch, "E90.17.6", {"start": v(309.3, -28.7) * mm, "end": v(308.5, -30.6) * mm});
            skLineSegment(sketch, "E90.18.0", {"start": v(314.63, -7.76) * mm, "end": v(305.48, -6.55) * mm});
            skLineSegment(sketch, "E90.18.1", {"start": v(315.65, 0) * mm, "end": v(314.36, -9.79) * mm});
            skLineSegment(sketch, "E90.18.2", {"start": v(314.1, -11.82) * mm, "end": v(304.94, -10.62) * mm});
            skCircle(sketch, "E90.18.3", {"center": v(305.21, -8.59) * mm, "radius": 2.05 * mm});
            skLineSegment(sketch, "E90.18.4", {"start": v(314.1, -11.82) * mm, "end": v(314.63, -7.76) * mm});
            skCircle(sketch, "E90.18.5", {"center": v(315.65, 0) * mm, "radius": 3.87 * mm});
            skLineSegment(sketch, "E90.18.6", {"start": v(314.36, -9.79) * mm, "end": v(314.1, -11.82) * mm});
            skLineSegment(sketch, "E90.19.0", {"start": v(314.1, 11.82) * mm, "end": v(304.94, 10.62) * mm});
            skLineSegment(sketch, "E90.19.1", {"start": v(313.07, 19.58) * mm, "end": v(314.36, 9.79) * mm});
            skLineSegment(sketch, "E90.19.2", {"start": v(314.63, 7.76) * mm, "end": v(305.48, 6.55) * mm});
            skCircle(sketch, "E90.19.3", {"center": v(305.21, 8.59) * mm, "radius": 2.05 * mm});
            skLineSegment(sketch, "E90.19.4", {"start": v(314.63, 7.76) * mm, "end": v(314.1, 11.82) * mm});
            skCircle(sketch, "E90.19.5", {"center": v(313.07, 19.58) * mm, "radius": 3.87 * mm});
            skLineSegment(sketch, "E90.19.6", {"start": v(314.36, 9.79) * mm, "end": v(314.63, 7.76) * mm});
            skLineSegment(sketch, "E90.20.0", {"start": v(308.5, 30.6) * mm, "end": v(299.98, 27.06) * mm});
            skLineSegment(sketch, "E90.20.1", {"start": v(305.51, 37.82) * mm, "end": v(309.3, 28.7) * mm});
            skLineSegment(sketch, "E90.20.2", {"start": v(310.08, 26.8) * mm, "end": v(301.55, 23.28) * mm});
            skCircle(sketch, "E90.20.3", {"center": v(300.77, 25.17) * mm, "radius": 2.05 * mm});
            skLineSegment(sketch, "E90.20.4", {"start": v(310.08, 26.8) * mm, "end": v(308.5, 30.6) * mm});
            skCircle(sketch, "E90.20.5", {"center": v(305.51, 37.82) * mm, "radius": 3.87 * mm});
            skLineSegment(sketch, "E90.20.6", {"start": v(309.3, 28.7) * mm, "end": v(310.08, 26.8) * mm});
            skLineSegment(sketch, "E90.21.0", {"start": v(298.25, 47.28) * mm, "end": v(290.93, 41.67) * mm});
            skLineSegment(sketch, "E90.21.1", {"start": v(293.5, 53.5) * mm, "end": v(299.5, 45.66) * mm});
            skLineSegment(sketch, "E90.21.2", {"start": v(300.75, 44.03) * mm, "end": v(293.43, 38.41) * mm});
            skCircle(sketch, "E90.21.3", {"center": v(292.18, 40.04) * mm, "radius": 2.05 * mm});
            skLineSegment(sketch, "E90.21.4", {"start": v(300.75, 44.03) * mm, "end": v(298.25, 47.28) * mm});
            skCircle(sketch, "E90.21.5", {"center": v(293.5, 53.5) * mm, "radius": 3.87 * mm});
            skLineSegment(sketch, "E90.21.6", {"start": v(299.5, 45.66) * mm, "end": v(300.75, 44.03) * mm});
            skLineSegment(sketch, "E90.22.0", {"start": v(284.03, 60.75) * mm, "end": v(278.41, 53.43) * mm});
            skLineSegment(sketch, "E90.22.1", {"start": v(277.82, 65.51) * mm, "end": v(285.66, 59.5) * mm});
            skLineSegment(sketch, "E90.22.2", {"start": v(287.28, 58.25) * mm, "end": v(281.67, 50.93) * mm});
            skCircle(sketch, "E90.22.3", {"center": v(280.04, 52.18) * mm, "radius": 2.05 * mm});
            skLineSegment(sketch, "E90.22.4", {"start": v(287.28, 58.25) * mm, "end": v(284.03, 60.75) * mm});
            skCircle(sketch, "E90.22.5", {"center": v(277.82, 65.51) * mm, "radius": 3.87 * mm});
            skLineSegment(sketch, "E90.22.6", {"start": v(285.66, 59.5) * mm, "end": v(287.28, 58.25) * mm});
            skLineSegment(sketch, "E90.23.0", {"start": v(266.8, 70.08) * mm, "end": v(263.28, 61.55) * mm});
            skLineSegment(sketch, "E90.23.1", {"start": v(259.58, 73.07) * mm, "end": v(268.7, 69.3) * mm});
            skLineSegment(sketch, "E90.23.2", {"start": v(270.6, 68.5) * mm, "end": v(267.06, 59.98) * mm});
            skCircle(sketch, "E90.23.3", {"center": v(265.17, 60.77) * mm, "radius": 2.05 * mm});
            skLineSegment(sketch, "E90.23.4", {"start": v(270.6, 68.5) * mm, "end": v(266.8, 70.08) * mm});
            skCircle(sketch, "E90.23.5", {"center": v(259.58, 73.07) * mm, "radius": 3.87 * mm});
            skLineSegment(sketch, "E90.23.6", {"start": v(268.7, 69.3) * mm, "end": v(270.6, 68.5) * mm});
            skLineSegment(sketch, "E91", {"start": v(250, 20.71) * mm, "end": v(250, 55.71) * mm});
            skLineSegment(sketch, "E92", {"start": v(260.71, 10) * mm, "end": v(295.71, 10) * mm});
            skLineSegment(sketch, "E93", {"start": v(240, 0) * mm, "end": v(250, 55.71) * mm, "construction": true});
            skArc(sketch, "E94", {"start": v(295.71, 10) * mm, "mid": v(280.02, 40.02) * mm, "end": v(250, 55.71) * mm});
            skArc(sketch, "E95.MirrorCS", {"start": v(184.29, 10) * mm, "mid": v(199.98, 40.02) * mm, "end": v(230, 55.71) * mm});
            skLineSegment(sketch, "E96.MirrorCS", {"start": v(230, 20.71) * mm, "end": v(230, 55.71) * mm});
            skLineSegment(sketch, "E97.MirrorCS", {"start": v(219.29, 10) * mm, "end": v(184.29, 10) * mm});
            skLineSegment(sketch, "E98.MirrorCS", {"start": v(260.71, -10) * mm, "end": v(295.71, -10) * mm});
            skArc(sketch, "E99.MirrorCS", {"start": v(295.71, -10) * mm, "mid": v(280.02, -40.02) * mm, "end": v(250, -55.71) * mm});
            skLineSegment(sketch, "E100.MirrorCS", {"start": v(250, -20.71) * mm, "end": v(250, -55.71) * mm});
            skLineSegment(sketch, "E101.MirrorCS", {"start": v(230, -20.71) * mm, "end": v(230, -55.71) * mm});
            skArc(sketch, "E102.MirrorCS", {"start": v(184.29, -10) * mm, "mid": v(199.98, -40.02) * mm, "end": v(230, -55.71) * mm});
            skLineSegment(sketch, "E103.MirrorCS", {"start": v(219.29, -10) * mm, "end": v(184.29, -10) * mm});
            skCircle(sketch, "E104", {"center": v(183.4, 0) * mm, "radius": 2.05 * mm});
            skCircle(sketch, "E105.MirrorC", {"center": v(296.6, 0) * mm, "radius": 2.05 * mm});
            skCircle(sketch, "E106", {"center": v(240, 56.6) * mm, "radius": 2.5 * mm});
            skCircle(sketch, "E107.MirrorC", {"center": v(240, -56.6) * mm, "radius": 2.5 * mm});
            skSolve(sketch);
        }
        {
            var Q0;
            {var subQ108=sQuery(id+"F0.wireOp",EDGE,"E7");Q0=makeQuery(id+"F0.imprint","IMPRINT",FACE,{"disambiguationData":[TD([[makeQuery(id+"F0.imprint","IMPRINT",EDGE,{"derivedFrom":subQ108}),-1.0]])]});}
            var Q1;
            Q1=makeQuery(id+"F0.imprint","IMPRINT",FACE,{"disambiguationData":[TD([[makeQuery(id+"F0.imprint","IMPRINT",EDGE,{"derivedFrom":sQuery(id+"F0.wireOp",EDGE,"E33")}),-1.0]])]});
            extrude(context, id + "F1", {"entities" : qUnion([Q0, Q1]), "depth" : 5 * mm, "offsetDistance" : 25 * mm});
        }
        {
            var Q0;
            Q0=makeQuery(id+"F0.imprint","IMPRINT",FACE,{"disambiguationData":[TD([[makeQuery(id+"F0.imprint","IMPRINT",EDGE,{"derivedFrom":sQuery(id+"F0.wireOp",EDGE,"E17.MirrorCS")}),-1.0]])]});
            var Q1;
            Q1=makeQuery(id+"F0.imprint","IMPRINT",FACE,{"disambiguationData":[TD([[makeQuery(id+"F0.imprint","IMPRINT",EDGE,{"derivedFrom":sQuery(id+"F0.wireOp",EDGE,"E11.bottom")}),1.0]])]});
            var Q2;
            Q2=makeQuery(id+"F0.imprint","IMPRINT",FACE,{"disambiguationData":[TD([[makeQuery(id+"F0.imprint","IMPRINT",EDGE,{"derivedFrom":sQuery(id+"F0.wireOp",EDGE,"E16.bottom")}),1.0]])]});
            var Q3;
            Q3=makeQuery(id+"F0.imprint","IMPRINT",FACE,{"disambiguationData":[TD([[makeQuery(id+"F0.imprint","IMPRINT",EDGE,{"derivedFrom":sQuery(id+"F0.wireOp",EDGE,"E12.MirrorCS")}),-1.0]])]});
            extrude(context, id + "F2", {"entities" : qUnion([Q0, Q1, Q2, Q3]), "operationType" : NewBodyOperationType.ADD, "depth" : 17 * mm, "offsetDistance" : 25 * mm});
        }
        {
            var Q0;
            Q0=makeQuery(id+"F0.imprint","IMPRINT",FACE,{"disambiguationData":[TD([[makeQuery(id+"F0.imprint","IMPRINT",EDGE,{"derivedFrom":sQuery(id+"F0.wireOp",EDGE,"E11.bottom")}),-1.0]])]});
            var Q1;
            Q1=makeQuery(id+"F0.imprint","IMPRINT",FACE,{"disambiguationData":[TD([[makeQuery(id+"F0.imprint","IMPRINT",EDGE,{"derivedFrom":sQuery(id+"F0.wireOp",EDGE,"E16.bottom")}),-1.0]])]});
            var Q2;
            Q2=makeQuery(id+"F0.imprint","IMPRINT",FACE,{"disambiguationData":[TD([[makeQuery(id+"F0.imprint","IMPRINT",EDGE,{"derivedFrom":sQuery(id+"F0.wireOp",EDGE,"E12.MirrorCS")}),1.0]])]});
            var Q3;
            Q3=makeQuery(id+"F0.imprint","IMPRINT",FACE,{"disambiguationData":[TD([[makeQuery(id+"F0.imprint","IMPRINT",EDGE,{"derivedFrom":sQuery(id+"F0.wireOp",EDGE,"E17.MirrorCS")}),1.0]])]});
            extrude(context, id + "F3", {"entities" : qUnion([Q0, Q1, Q2, Q3]), "operationType" : NewBodyOperationType.ADD, "depth" : 33 * mm, "offsetDistance" : 25 * mm});
        }
        {
            var Q0;
            Q0=makeQuery(id+"F1.opExtrude","SWEPT_EDGE",EDGE,{"disambiguationData":[OSD([sQuery(id+"F0.wireOp",EDGE,"E4"),sQuery(id+"F0.wireOp",EDGE,"E10.23.0")])]});
            var Q1;
            Q1=makeQuery(id+"F1.opExtrude","SWEPT_EDGE",EDGE,{"disambiguationData":[OSD([sQuery(id+"F0.wireOp",EDGE,"E6.MirrorCS"),sQuery(id+"F0.wireOp",EDGE,"E10.23.0")])]});
            var Q2;
            Q2=makeQuery(id+"F1.opExtrude","SWEPT_EDGE",EDGE,{"disambiguationData":[OSD([sQuery(id+"F0.wireOp",EDGE,"E10.23.0"),sQuery(id+"F0.wireOp",EDGE,"E10.23.1")])]});
            var Q3;
            Q3=makeQuery(id+"F1.opExtrude","SWEPT_EDGE",EDGE,{"disambiguationData":[OSD([sQuery(id+"F0.wireOp",EDGE,"E10.23.0"),sQuery(id+"F0.wireOp",EDGE,"E10.23.2")])]});
            var Q4;
            Q4=makeQuery(id+"F1.opExtrude","SWEPT_EDGE",EDGE,{"disambiguationData":[OSD([sQuery(id+"F0.wireOp",EDGE,"E10.22.1"),sQuery(id+"F0.wireOp",EDGE,"E10.23.0")])]});
            var Q5;
            Q5=makeQuery(id+"F1.opExtrude","SWEPT_EDGE",EDGE,{"disambiguationData":[OSD([sQuery(id+"F0.wireOp",EDGE,"E10.22.2"),sQuery(id+"F0.wireOp",EDGE,"E10.23.0")])]});
            var Q6;
            Q6=makeQuery(id+"F1.opExtrude","SWEPT_EDGE",EDGE,{"disambiguationData":[OSD([sQuery(id+"F0.wireOp",EDGE,"E10.21.1"),sQuery(id+"F0.wireOp",EDGE,"E10.23.0")])]});
            var Q7;
            Q7=makeQuery(id+"F1.opExtrude","SWEPT_EDGE",EDGE,{"disambiguationData":[OSD([sQuery(id+"F0.wireOp",EDGE,"E10.21.2"),sQuery(id+"F0.wireOp",EDGE,"E10.23.0")])]});
            var Q8;
            Q8=makeQuery(id+"F1.opExtrude","SWEPT_EDGE",EDGE,{"disambiguationData":[OSD([sQuery(id+"F0.wireOp",EDGE,"E10.1.2"),sQuery(id+"F0.wireOp",EDGE,"E10.23.0")])]});
            var Q9;
            Q9=makeQuery(id+"F1.opExtrude","SWEPT_EDGE",EDGE,{"disambiguationData":[OSD([sQuery(id+"F0.wireOp",EDGE,"E10.1.1"),sQuery(id+"F0.wireOp",EDGE,"E10.23.0")])]});
            var Q10;
            Q10=makeQuery(id+"F1.opExtrude","SWEPT_EDGE",EDGE,{"disambiguationData":[OSD([sQuery(id+"F0.wireOp",EDGE,"E10.2.2"),sQuery(id+"F0.wireOp",EDGE,"E10.23.0")])]});
            var Q11;
            Q11=makeQuery(id+"F1.opExtrude","SWEPT_EDGE",EDGE,{"disambiguationData":[OSD([sQuery(id+"F0.wireOp",EDGE,"E10.2.1"),sQuery(id+"F0.wireOp",EDGE,"E10.23.0")])]});
            var Q12;
            Q12=makeQuery(id+"F1.opExtrude","SWEPT_EDGE",EDGE,{"disambiguationData":[OSD([sQuery(id+"F0.wireOp",EDGE,"E10.3.2"),sQuery(id+"F0.wireOp",EDGE,"E10.23.0")])]});
            var Q13;
            Q13=makeQuery(id+"F1.opExtrude","SWEPT_EDGE",EDGE,{"disambiguationData":[OSD([sQuery(id+"F0.wireOp",EDGE,"E10.3.1"),sQuery(id+"F0.wireOp",EDGE,"E10.23.0")])]});
            var Q14;
            Q14=makeQuery(id+"F1.opExtrude","SWEPT_EDGE",EDGE,{"disambiguationData":[OSD([sQuery(id+"F0.wireOp",EDGE,"E10.4.2"),sQuery(id+"F0.wireOp",EDGE,"E10.23.0")])]});
            var Q15;
            Q15=makeQuery(id+"F1.opExtrude","SWEPT_EDGE",EDGE,{"disambiguationData":[OSD([sQuery(id+"F0.wireOp",EDGE,"E10.4.1"),sQuery(id+"F0.wireOp",EDGE,"E10.23.0")])]});
            var Q16;
            Q16=makeQuery(id+"F1.opExtrude","SWEPT_EDGE",EDGE,{"disambiguationData":[OSD([sQuery(id+"F0.wireOp",EDGE,"E10.5.2"),sQuery(id+"F0.wireOp",EDGE,"E10.23.0")])]});
            var Q17;
            Q17=makeQuery(id+"F1.opExtrude","SWEPT_EDGE",EDGE,{"disambiguationData":[OSD([sQuery(id+"F0.wireOp",EDGE,"E10.5.1"),sQuery(id+"F0.wireOp",EDGE,"E10.23.0")])]});
            var Q18;
            Q18=makeQuery(id+"F1.opExtrude","SWEPT_EDGE",EDGE,{"disambiguationData":[OSD([sQuery(id+"F0.wireOp",EDGE,"E10.20.1"),sQuery(id+"F0.wireOp",EDGE,"E10.23.0")])]});
            var Q19;
            Q19=makeQuery(id+"F1.opExtrude","SWEPT_EDGE",EDGE,{"disambiguationData":[OSD([sQuery(id+"F0.wireOp",EDGE,"E10.20.2"),sQuery(id+"F0.wireOp",EDGE,"E10.23.0")])]});
            var Q20;
            Q20=makeQuery(id+"F1.opExtrude","SWEPT_EDGE",EDGE,{"disambiguationData":[OSD([sQuery(id+"F0.wireOp",EDGE,"E10.19.1"),sQuery(id+"F0.wireOp",EDGE,"E10.23.0")])]});
            var Q21;
            Q21=makeQuery(id+"F1.opExtrude","SWEPT_EDGE",EDGE,{"disambiguationData":[OSD([sQuery(id+"F0.wireOp",EDGE,"E10.19.2"),sQuery(id+"F0.wireOp",EDGE,"E10.23.0")])]});
            var Q22;
            Q22=makeQuery(id+"F1.opExtrude","SWEPT_EDGE",EDGE,{"disambiguationData":[OSD([sQuery(id+"F0.wireOp",EDGE,"E10.18.1"),sQuery(id+"F0.wireOp",EDGE,"E10.23.0")])]});
            var Q23;
            Q23=makeQuery(id+"F1.opExtrude","SWEPT_EDGE",EDGE,{"disambiguationData":[OSD([sQuery(id+"F0.wireOp",EDGE,"E10.18.2"),sQuery(id+"F0.wireOp",EDGE,"E10.23.0")])]});
            var Q24;
            Q24=makeQuery(id+"F1.opExtrude","SWEPT_EDGE",EDGE,{"disambiguationData":[OSD([sQuery(id+"F0.wireOp",EDGE,"E10.17.1"),sQuery(id+"F0.wireOp",EDGE,"E10.23.0")])]});
            var Q25;
            Q25=makeQuery(id+"F1.opExtrude","SWEPT_EDGE",EDGE,{"disambiguationData":[OSD([sQuery(id+"F0.wireOp",EDGE,"E10.17.2"),sQuery(id+"F0.wireOp",EDGE,"E10.23.0")])]});
            var Q26;
            Q26=makeQuery(id+"F1.opExtrude","SWEPT_EDGE",EDGE,{"disambiguationData":[OSD([sQuery(id+"F0.wireOp",EDGE,"E10.16.1"),sQuery(id+"F0.wireOp",EDGE,"E10.23.0")])]});
            var Q27;
            Q27=makeQuery(id+"F1.opExtrude","SWEPT_EDGE",EDGE,{"disambiguationData":[OSD([sQuery(id+"F0.wireOp",EDGE,"E10.16.2"),sQuery(id+"F0.wireOp",EDGE,"E10.23.0")])]});
            var Q28;
            Q28=makeQuery(id+"F1.opExtrude","SWEPT_EDGE",EDGE,{"disambiguationData":[OSD([sQuery(id+"F0.wireOp",EDGE,"E10.15.1"),sQuery(id+"F0.wireOp",EDGE,"E10.23.0")])]});
            var Q29;
            Q29=makeQuery(id+"F1.opExtrude","SWEPT_EDGE",EDGE,{"disambiguationData":[OSD([sQuery(id+"F0.wireOp",EDGE,"E10.15.2"),sQuery(id+"F0.wireOp",EDGE,"E10.23.0")])]});
            var Q30;
            {var subQ0=sQuery(id+"F0.wireOp",EDGE,"E10.23.0");var subQ1=sQuery(id+"F0.wireOp",EDGE,"E10.15.4");Q30=makeQuery(id+"F1.opExtrude","SWEPT_EDGE",EDGE,{"disambiguationData":[OSD([subQ1,subQ0]),TDD([makeQuery(id+"F0.imprint","INTERSECT",VERTEX,{"disambiguationData":[OD(0.0)],"derivedFrom":[subQ1,subQ0]})])]});}
            var Q31;
            Q31=makeQuery(id+"F1.opExtrude","SWEPT_EDGE",EDGE,{"disambiguationData":[OSD([sQuery(id+"F0.wireOp",EDGE,"E10.14.2"),sQuery(id+"F0.wireOp",EDGE,"E10.23.0")])]});
            var Q32;
            {var subQ0=sQuery(id+"F0.wireOp",EDGE,"E10.23.0");var subQ1=sQuery(id+"F0.wireOp",EDGE,"E10.14.4");Q32=makeQuery(id+"F1.opExtrude","SWEPT_EDGE",EDGE,{"disambiguationData":[OSD([subQ1,subQ0]),TDD([makeQuery(id+"F0.imprint","INTERSECT",VERTEX,{"disambiguationData":[OD(0.0)],"derivedFrom":[subQ1,subQ0]})])]});}
            var Q33;
            Q33=makeQuery(id+"F1.opExtrude","SWEPT_EDGE",EDGE,{"disambiguationData":[OSD([sQuery(id+"F0.wireOp",EDGE,"E10.13.2"),sQuery(id+"F0.wireOp",EDGE,"E10.23.0")])]});
            var Q34;
            Q34=makeQuery(id+"F1.opExtrude","SWEPT_EDGE",EDGE,{"disambiguationData":[OSD([sQuery(id+"F0.wireOp",EDGE,"E10.12.1"),sQuery(id+"F0.wireOp",EDGE,"E10.23.0")])]});
            var Q35;
            Q35=makeQuery(id+"F1.opExtrude","SWEPT_EDGE",EDGE,{"disambiguationData":[OSD([sQuery(id+"F0.wireOp",EDGE,"E10.12.2"),sQuery(id+"F0.wireOp",EDGE,"E10.23.0")])]});
            var Q36;
            Q36=makeQuery(id+"F1.opExtrude","SWEPT_EDGE",EDGE,{"disambiguationData":[OSD([sQuery(id+"F0.wireOp",EDGE,"E10.11.1"),sQuery(id+"F0.wireOp",EDGE,"E10.23.0")])]});
            var Q37;
            Q37=makeQuery(id+"F1.opExtrude","SWEPT_EDGE",EDGE,{"disambiguationData":[OSD([sQuery(id+"F0.wireOp",EDGE,"E10.11.2"),sQuery(id+"F0.wireOp",EDGE,"E10.23.0")])]});
            var Q38;
            Q38=makeQuery(id+"F1.opExtrude","SWEPT_EDGE",EDGE,{"disambiguationData":[OSD([sQuery(id+"F0.wireOp",EDGE,"E10.10.1"),sQuery(id+"F0.wireOp",EDGE,"E10.23.0")])]});
            var Q39;
            Q39=makeQuery(id+"F1.opExtrude","SWEPT_EDGE",EDGE,{"disambiguationData":[OSD([sQuery(id+"F0.wireOp",EDGE,"E10.10.2"),sQuery(id+"F0.wireOp",EDGE,"E10.23.0")])]});
            var Q40;
            Q40=makeQuery(id+"F1.opExtrude","SWEPT_EDGE",EDGE,{"disambiguationData":[OSD([sQuery(id+"F0.wireOp",EDGE,"E10.9.1"),sQuery(id+"F0.wireOp",EDGE,"E10.23.0")])]});
            var Q41;
            Q41=makeQuery(id+"F1.opExtrude","SWEPT_EDGE",EDGE,{"disambiguationData":[OSD([sQuery(id+"F0.wireOp",EDGE,"E10.9.2"),sQuery(id+"F0.wireOp",EDGE,"E10.23.0")])]});
            var Q42;
            Q42=makeQuery(id+"F1.opExtrude","SWEPT_EDGE",EDGE,{"disambiguationData":[OSD([sQuery(id+"F0.wireOp",EDGE,"E10.8.1"),sQuery(id+"F0.wireOp",EDGE,"E10.23.0")])]});
            var Q43;
            Q43=makeQuery(id+"F1.opExtrude","SWEPT_EDGE",EDGE,{"disambiguationData":[OSD([sQuery(id+"F0.wireOp",EDGE,"E10.8.2"),sQuery(id+"F0.wireOp",EDGE,"E10.23.0")])]});
            var Q44;
            Q44=makeQuery(id+"F1.opExtrude","SWEPT_EDGE",EDGE,{"disambiguationData":[OSD([sQuery(id+"F0.wireOp",EDGE,"E10.6.2"),sQuery(id+"F0.wireOp",EDGE,"E10.23.0")])]});
            var Q45;
            Q45=makeQuery(id+"F1.opExtrude","SWEPT_EDGE",EDGE,{"disambiguationData":[OSD([sQuery(id+"F0.wireOp",EDGE,"E10.6.1"),sQuery(id+"F0.wireOp",EDGE,"E10.23.0")])]});
            var Q46;
            Q46=makeQuery(id+"F1.opExtrude","SWEPT_EDGE",EDGE,{"disambiguationData":[OSD([sQuery(id+"F0.wireOp",EDGE,"E10.7.2"),sQuery(id+"F0.wireOp",EDGE,"E10.23.0")])]});
            var Q47;
            Q47=makeQuery(id+"F1.opExtrude","SWEPT_EDGE",EDGE,{"disambiguationData":[OSD([sQuery(id+"F0.wireOp",EDGE,"E10.7.1"),sQuery(id+"F0.wireOp",EDGE,"E10.23.0")])]});
            var Q48;
            Q48=makeQuery(id+"F1.opExtrude","SWEPT_EDGE",EDGE,{"disambiguationData":[OSD([sQuery(id+"F0.wireOp",EDGE,"E10.14.1"),sQuery(id+"F0.wireOp",EDGE,"E74.4.23.0")])]});
            var Q49;
            Q49=makeQuery(id+"F1.opExtrude","SWEPT_EDGE",EDGE,{"disambiguationData":[OSD([sQuery(id+"F0.wireOp",EDGE,"E10.13.1"),sQuery(id+"F0.wireOp",EDGE,"E74.4.23.0")])]});
            var Q50;
            Q50=makeQuery(id+"F1.opExtrude","SWEPT_EDGE",EDGE,{"disambiguationData":[OSD([sQuery(id+"F0.wireOp",EDGE,"E74.5.15.0"),sQuery(id+"F0.wireOp",EDGE,"E74.4.23.0")])]});
            var Q51;
            Q51=makeQuery(id+"F1.opExtrude","SWEPT_EDGE",EDGE,{"disambiguationData":[OSD([sQuery(id+"F0.wireOp",EDGE,"E74.2.15.0"),sQuery(id+"F0.wireOp",EDGE,"E74.4.23.0")])]});
            var Q52;
            Q52=makeQuery(id+"F1.opExtrude","SWEPT_EDGE",EDGE,{"disambiguationData":[OSD([sQuery(id+"F0.wireOp",EDGE,"E74.5.16.0"),sQuery(id+"F0.wireOp",EDGE,"E74.4.23.0")])]});
            var Q53;
            Q53=makeQuery(id+"F1.opExtrude","SWEPT_EDGE",EDGE,{"disambiguationData":[OSD([sQuery(id+"F0.wireOp",EDGE,"E74.2.16.0"),sQuery(id+"F0.wireOp",EDGE,"E74.4.23.0")])]});
            var Q54;
            Q54=makeQuery(id+"F1.opExtrude","SWEPT_EDGE",EDGE,{"disambiguationData":[OSD([sQuery(id+"F0.wireOp",EDGE,"E74.5.17.0"),sQuery(id+"F0.wireOp",EDGE,"E74.4.23.0")])]});
            var Q55;
            Q55=makeQuery(id+"F1.opExtrude","SWEPT_EDGE",EDGE,{"disambiguationData":[OSD([sQuery(id+"F0.wireOp",EDGE,"E74.2.17.0"),sQuery(id+"F0.wireOp",EDGE,"E74.4.23.0")])]});
            var Q56;
            Q56=makeQuery(id+"F1.opExtrude","SWEPT_EDGE",EDGE,{"disambiguationData":[OSD([sQuery(id+"F0.wireOp",EDGE,"E74.5.18.0"),sQuery(id+"F0.wireOp",EDGE,"E74.4.23.0")])]});
            var Q57;
            Q57=makeQuery(id+"F1.opExtrude","SWEPT_EDGE",EDGE,{"disambiguationData":[OSD([sQuery(id+"F0.wireOp",EDGE,"E74.2.18.0"),sQuery(id+"F0.wireOp",EDGE,"E74.4.23.0")])]});
            var Q58;
            Q58=makeQuery(id+"F1.opExtrude","SWEPT_EDGE",EDGE,{"disambiguationData":[OSD([sQuery(id+"F0.wireOp",EDGE,"E74.5.19.0"),sQuery(id+"F0.wireOp",EDGE,"E74.4.23.0")])]});
            var Q59;
            Q59=makeQuery(id+"F1.opExtrude","SWEPT_EDGE",EDGE,{"disambiguationData":[OSD([sQuery(id+"F0.wireOp",EDGE,"E74.2.19.0"),sQuery(id+"F0.wireOp",EDGE,"E74.4.23.0")])]});
            var Q60;
            Q60=makeQuery(id+"F1.opExtrude","SWEPT_EDGE",EDGE,{"disambiguationData":[OSD([sQuery(id+"F0.wireOp",EDGE,"E74.5.20.0"),sQuery(id+"F0.wireOp",EDGE,"E74.4.23.0")])]});
            var Q61;
            Q61=makeQuery(id+"F1.opExtrude","SWEPT_EDGE",EDGE,{"disambiguationData":[OSD([sQuery(id+"F0.wireOp",EDGE,"E74.2.20.0"),sQuery(id+"F0.wireOp",EDGE,"E74.4.23.0")])]});
            var Q62;
            Q62=makeQuery(id+"F1.opExtrude","SWEPT_EDGE",EDGE,{"disambiguationData":[OSD([sQuery(id+"F0.wireOp",EDGE,"E74.2.21.0"),sQuery(id+"F0.wireOp",EDGE,"E74.4.23.0")])]});
            var Q63;
            Q63=makeQuery(id+"F1.opExtrude","SWEPT_EDGE",EDGE,{"disambiguationData":[OSD([sQuery(id+"F0.wireOp",EDGE,"E74.5.21.0"),sQuery(id+"F0.wireOp",EDGE,"E74.4.23.0")])]});
            var Q64;
            Q64=makeQuery(id+"F1.opExtrude","SWEPT_EDGE",EDGE,{"disambiguationData":[OSD([sQuery(id+"F0.wireOp",EDGE,"E74.5.22.0"),sQuery(id+"F0.wireOp",EDGE,"E74.4.23.0")])]});
            var Q65;
            Q65=makeQuery(id+"F1.opExtrude","SWEPT_EDGE",EDGE,{"disambiguationData":[OSD([sQuery(id+"F0.wireOp",EDGE,"E74.2.22.0"),sQuery(id+"F0.wireOp",EDGE,"E74.4.23.0")])]});
            var Q66;
            Q66=makeQuery(id+"F1.opExtrude","SWEPT_EDGE",EDGE,{"disambiguationData":[OSD([sQuery(id+"F0.wireOp",EDGE,"E74.2.23.0"),sQuery(id+"F0.wireOp",EDGE,"E74.4.23.0")])]});
            var Q67;
            Q67=makeQuery(id+"F1.opExtrude","SWEPT_EDGE",EDGE,{"disambiguationData":[OSD([sQuery(id+"F0.wireOp",EDGE,"E74.4.23.0"),sQuery(id+"F0.wireOp",EDGE,"E74.5.23.0")])]});
            var Q68;
            Q68=makeQuery(id+"F1.opExtrude","SWEPT_EDGE",EDGE,{"disambiguationData":[OSD([sQuery(id+"F0.wireOp",EDGE,"E0"),sQuery(id+"F0.wireOp",EDGE,"E79")])]});
            fillet(context, id + "F4", {"entities" : qUnion([Q0, Q1, Q2, Q3, Q4, Q5, Q6, Q7, Q8, Q9, Q10, Q11, Q12, Q13, Q14, Q15, Q16, Q17, Q18, Q19, Q20, Q21, Q22, Q23, Q24, Q25, Q26, Q27, Q28, Q29, Q30, Q31, Q32, Q33, Q34, Q35, Q36, Q37, Q38, Q39, Q40, Q41, Q42, Q43, Q44, Q45, Q46, Q47, Q48, Q49, Q50, Q51, Q52, Q53, Q54, Q55, Q56, Q57, Q58, Q59, Q60, Q61, Q62, Q63, Q64, Q65, Q66, Q67, Q68]), "radius" : 2 * mm, "tangentPropagation" : true, "allowEdgeOverflow" : false});
        }
        {
            var Q0;
            Q0=makeQuery(id+"F0.imprint","IMPRINT",FACE,{"disambiguationData":[TD([[makeQuery(id+"F0.imprint","IMPRINT",EDGE,{"derivedFrom":sQuery(id+"F0.wireOp",EDGE,"E32")}),-1.0]])]});
            extrude(context, id + "F5", {"entities" : qUnion([Q0]), "operationType" : NewBodyOperationType.ADD, "oppositeDirection" : true, "depth" : 13 * mm, "offsetDistance" : 25 * mm, "hasSecondDirection" : true, "secondDirectionOppositeDirection" : false, "secondDirectionDepth" : 5 * mm});
        }
        {
            var Q0;
            Q0=makeQuery(id+"F0.imprint","IMPRINT",FACE,{"disambiguationData":[TD([[makeQuery(id+"F0.imprint","IMPRINT",EDGE,{"derivedFrom":sQuery(id+"F0.wireOp",EDGE,"E31")}),-1.0]])]});
            extrude(context, id + "F6", {"entities" : qUnion([Q0]), "operationType" : NewBodyOperationType.ADD, "oppositeDirection" : true, "depth" : 2 * mm, "offsetDistance" : 25 * mm});
        }
        {
            var Q0;
            Q0=makeQuery(id+"F0.imprint","IMPRINT",FACE,{"disambiguationData":[TD([[makeQuery(id+"F0.imprint","IMPRINT",EDGE,{"derivedFrom":sQuery(id+"F0.wireOp",EDGE,"E31")}),1.0]])]});
            var Q1;
            Q1=makeQuery(id+"F0.imprint","IMPRINT",FACE,{"disambiguationData":[TD([[makeQuery(id+"F0.imprint","IMPRINT",EDGE,{"derivedFrom":sQuery(id+"F0.wireOp",EDGE,"E31")}),-1.0]])]});
            extrude(context, id + "F7", {"entities" : qUnion([Q0, Q1]), "operationType" : NewBodyOperationType.ADD, "depth" : 5 * mm, "offsetDistance" : 25 * mm});
        }
        {
            var Q0;
            {var subQ6=sQuery(id+"F0.wireOp",EDGE,"E26.MirrorCS");Q0=makeQuery(id+"F0.imprint","IMPRINT",FACE,{"disambiguationData":[TD([[makeQuery(id+"F0.imprint","IMPRINT",EDGE,{"derivedFrom":subQ6}),-1.0]])]});}
            var Q1;
            {var subQ0=sQuery(id+"F0.wireOp",EDGE,"E62.MirrorCS");var subQ1=sQuery(id+"F0.wireOp",EDGE,"E33");var subQ2=makeQuery(id+"F0.imprint","INTERSECT",VERTEX,{"derivedFrom":[subQ1,subQ0]});Q1=makeQuery(id+"F0.imprint","IMPRINT",FACE,{"disambiguationData":[TD([[makeQuery(id+"F0.imprint","IMPRINT",EDGE,{"disambiguationData":[TD([[subQ2,1.0]])],"derivedFrom":subQ1}),-1.0]])]});}
            var Q2;
            {var subQ0=sQuery(id+"F0.wireOp",EDGE,"E30.MirrorCS");Q2=makeQuery(id+"F0.imprint","IMPRINT",FACE,{"disambiguationData":[TD([[makeQuery(id+"F0.imprint","IMPRINT",EDGE,{"derivedFrom":subQ0}),-1.0]])]});}
            var Q3;
            {var subQ1=sQuery(id+"F0.wireOp",EDGE,"E27.MirrorCS");Q3=makeQuery(id+"F0.imprint","IMPRINT",FACE,{"disambiguationData":[TD([[makeQuery(id+"F0.imprint","IMPRINT",EDGE,{"derivedFrom":subQ1}),-1.0]])]});}
            var Q4;
            {var subQ1=sQuery(id+"F0.wireOp",EDGE,"E29.MirrorCS");Q4=makeQuery(id+"F0.imprint","IMPRINT",FACE,{"disambiguationData":[TD([[makeQuery(id+"F0.imprint","IMPRINT",EDGE,{"derivedFrom":subQ1}),1.0]])]});}
            var Q5;
            {var subQ1=sQuery(id+"F0.wireOp",EDGE,"E22.bottom");Q5=makeQuery(id+"F0.imprint","IMPRINT",FACE,{"disambiguationData":[TD([[makeQuery(id+"F0.imprint","IMPRINT",EDGE,{"derivedFrom":subQ1}),1.0]])]});}
            var Q6;
            {var subQ0=sQuery(id+"F0.wireOp",EDGE,"E22.right");Q6=makeQuery(id+"F0.imprint","IMPRINT",FACE,{"disambiguationData":[TD([[makeQuery(id+"F0.imprint","IMPRINT",EDGE,{"derivedFrom":subQ0}),1.0]])]});}
            var Q7;
            {var subQ1=sQuery(id+"F0.wireOp",EDGE,"E22.top");Q7=makeQuery(id+"F0.imprint","IMPRINT",FACE,{"disambiguationData":[TD([[makeQuery(id+"F0.imprint","IMPRINT",EDGE,{"derivedFrom":subQ1}),-1.0]])]});}
            var Q8;
            {var subQ1=sQuery(id+"F0.wireOp",EDGE,"E21.left");Q8=makeQuery(id+"F0.imprint","IMPRINT",FACE,{"disambiguationData":[TD([[makeQuery(id+"F0.imprint","IMPRINT",EDGE,{"derivedFrom":subQ1}),-1.0]])]});}
            var Q9;
            {var subQ0=sQuery(id+"F0.wireOp",EDGE,"E21.bottom");Q9=makeQuery(id+"F0.imprint","IMPRINT",FACE,{"disambiguationData":[TD([[makeQuery(id+"F0.imprint","IMPRINT",EDGE,{"derivedFrom":subQ0}),1.0]])]});}
            var Q10;
            {var subQ4=sQuery(id+"F0.wireOp",EDGE,"E21.right");Q10=makeQuery(id+"F0.imprint","IMPRINT",FACE,{"disambiguationData":[TD([[makeQuery(id+"F0.imprint","IMPRINT",EDGE,{"derivedFrom":subQ4}),1.0]])]});}
            var Q11;
            {var subQ1=sQuery(id+"F0.wireOp",EDGE,"E23.MirrorCS");Q11=makeQuery(id+"F0.imprint","IMPRINT",FACE,{"disambiguationData":[TD([[makeQuery(id+"F0.imprint","IMPRINT",EDGE,{"derivedFrom":subQ1}),1.0]])]});}
            var Q12;
            {var subQ0=sQuery(id+"F0.wireOp",EDGE,"E25.MirrorCS");Q12=makeQuery(id+"F0.imprint","IMPRINT",FACE,{"disambiguationData":[TD([[makeQuery(id+"F0.imprint","IMPRINT",EDGE,{"derivedFrom":subQ0}),-1.0]])]});}
            var Q13;
            {var subQ5=sQuery(id+"F0.wireOp",EDGE,"E65.MirrorCS");var subQ7=sQuery(id+"F0.wireOp",EDGE,"E33");var subQ8=makeQuery(id+"F0.imprint","INTERSECT",VERTEX,{"derivedFrom":[subQ7,subQ5]});Q13=makeQuery(id+"F0.imprint","IMPRINT",FACE,{"disambiguationData":[TD([[makeQuery(id+"F0.imprint","IMPRINT",EDGE,{"disambiguationData":[TD([[subQ8,1.0]])],"derivedFrom":subQ7}),-1.0]])]});}
            var Q14;
            {var subQ5=sQuery(id+"F0.wireOp",EDGE,"E61.MirrorCS");var subQ7=sQuery(id+"F0.wireOp",EDGE,"E33");var subQ8=makeQuery(id+"F0.imprint","INTERSECT",VERTEX,{"derivedFrom":[subQ7,subQ5]});Q14=makeQuery(id+"F0.imprint","IMPRINT",FACE,{"disambiguationData":[TD([[makeQuery(id+"F0.imprint","IMPRINT",EDGE,{"disambiguationData":[TD([[subQ8,-1.0]])],"derivedFrom":subQ7}),-1.0]])]});}
            var Q15;
            {var subQ0=sQuery(id+"F0.wireOp",EDGE,"E70.MirrorCS");var subQ1=sQuery(id+"F0.wireOp",EDGE,"E33");var subQ2=makeQuery(id+"F0.imprint","INTERSECT",VERTEX,{"derivedFrom":[subQ1,subQ0]});Q15=makeQuery(id+"F0.imprint","IMPRINT",FACE,{"disambiguationData":[TD([[makeQuery(id+"F0.imprint","IMPRINT",EDGE,{"disambiguationData":[TD([[subQ2,1.0]])],"derivedFrom":subQ1}),-1.0]])]});}
            var Q16;
            {var subQ0=sQuery(id+"F0.wireOp",EDGE,"E71.MirrorCS");var subQ1=sQuery(id+"F0.wireOp",EDGE,"E33");var subQ2=makeQuery(id+"F0.imprint","INTERSECT",VERTEX,{"derivedFrom":[subQ1,subQ0]});Q16=makeQuery(id+"F0.imprint","IMPRINT",FACE,{"disambiguationData":[TD([[makeQuery(id+"F0.imprint","IMPRINT",EDGE,{"disambiguationData":[TD([[subQ2,1.0]])],"derivedFrom":subQ1}),-1.0]])]});}
            var Q17;
            {var subQ0=sQuery(id+"F0.wireOp",EDGE,"E72.MirrorCS");var subQ1=sQuery(id+"F0.wireOp",EDGE,"E33");var subQ2=makeQuery(id+"F0.imprint","INTERSECT",VERTEX,{"derivedFrom":[subQ1,subQ0]});Q17=makeQuery(id+"F0.imprint","IMPRINT",FACE,{"disambiguationData":[TD([[makeQuery(id+"F0.imprint","IMPRINT",EDGE,{"disambiguationData":[TD([[subQ2,1.0]])],"derivedFrom":subQ1}),-1.0]])]});}
            var Q18;
            {var subQ0=sQuery(id+"F0.wireOp",EDGE,"E60.MirrorCS");var subQ1=sQuery(id+"F0.wireOp",EDGE,"E33");var subQ2=makeQuery(id+"F0.imprint","INTERSECT",VERTEX,{"derivedFrom":[subQ1,subQ0]});Q18=makeQuery(id+"F0.imprint","IMPRINT",FACE,{"disambiguationData":[TD([[makeQuery(id+"F0.imprint","IMPRINT",EDGE,{"disambiguationData":[TD([[subQ2,-1.0]])],"derivedFrom":subQ1}),-1.0]])]});}
            var Q19;
            {var subQ0=sQuery(id+"F0.wireOp",EDGE,"E58");var subQ1=sQuery(id+"F0.wireOp",EDGE,"E33");var subQ2=makeQuery(id+"F0.imprint","INTERSECT",VERTEX,{"derivedFrom":[subQ1,subQ0]});Q19=makeQuery(id+"F0.imprint","IMPRINT",FACE,{"disambiguationData":[TD([[makeQuery(id+"F0.imprint","IMPRINT",EDGE,{"disambiguationData":[TD([[subQ2,-1.0]])],"derivedFrom":subQ1}),-1.0]])]});}
            var Q20;
            {var subQ0=sQuery(id+"F0.wireOp",EDGE,"E64.MirrorCS");var subQ1=sQuery(id+"F0.wireOp",EDGE,"E33");var subQ2=makeQuery(id+"F0.imprint","INTERSECT",VERTEX,{"derivedFrom":[subQ1,subQ0]});Q20=makeQuery(id+"F0.imprint","IMPRINT",FACE,{"disambiguationData":[TD([[makeQuery(id+"F0.imprint","IMPRINT",EDGE,{"disambiguationData":[TD([[subQ2,1.0]])],"derivedFrom":subQ1}),-1.0]])]});}
            var Q21;
            {var subQ0=sQuery(id+"F0.wireOp",EDGE,"E63.MirrorCS");var subQ1=sQuery(id+"F0.wireOp",EDGE,"E33");var subQ2=makeQuery(id+"F0.imprint","INTERSECT",VERTEX,{"derivedFrom":[subQ1,subQ0]});Q21=makeQuery(id+"F0.imprint","IMPRINT",FACE,{"disambiguationData":[TD([[makeQuery(id+"F0.imprint","IMPRINT",EDGE,{"disambiguationData":[TD([[subQ2,1.0]])],"derivedFrom":subQ1}),-1.0]])]});}
            var Q22;
            {var subQ0=sQuery(id+"F0.wireOp",EDGE,"E58");var subQ1=sQuery(id+"F0.wireOp",EDGE,"E33");var subQ2=makeQuery(id+"F0.imprint","INTERSECT",VERTEX,{"derivedFrom":[subQ1,subQ0]});Q22=makeQuery(id+"F0.imprint","IMPRINT",FACE,{"disambiguationData":[TD([[makeQuery(id+"F0.imprint","IMPRINT",EDGE,{"disambiguationData":[TD([[subQ2,1.0]])],"derivedFrom":subQ1}),-1.0]])]});}
            var Q23;
            {var subQ2=sQuery(id+"F0.wireOp",EDGE,"E59");var subQ7=sQuery(id+"F0.wireOp",EDGE,"E33");var subQ8=makeQuery(id+"F0.imprint","INTERSECT",VERTEX,{"derivedFrom":[subQ7,subQ2]});Q23=makeQuery(id+"F0.imprint","IMPRINT",FACE,{"disambiguationData":[TD([[makeQuery(id+"F0.imprint","IMPRINT",EDGE,{"disambiguationData":[TD([[subQ8,1.0]])],"derivedFrom":subQ7}),-1.0]])]});}
            var Q24;
            {var subQ0=sQuery(id+"F0.wireOp",EDGE,"E67");var subQ1=sQuery(id+"F0.wireOp",EDGE,"E33");var subQ2=makeQuery(id+"F0.imprint","INTERSECT",VERTEX,{"derivedFrom":[subQ1,subQ0]});Q24=makeQuery(id+"F0.imprint","IMPRINT",FACE,{"disambiguationData":[TD([[makeQuery(id+"F0.imprint","IMPRINT",EDGE,{"disambiguationData":[TD([[subQ2,-1.0]])],"derivedFrom":subQ1}),-1.0]])]});}
            var Q25;
            {var subQ0=sQuery(id+"F0.wireOp",EDGE,"E66");var subQ1=sQuery(id+"F0.wireOp",EDGE,"E33");var subQ2=makeQuery(id+"F0.imprint","INTERSECT",VERTEX,{"derivedFrom":[subQ1,subQ0]});Q25=makeQuery(id+"F0.imprint","IMPRINT",FACE,{"disambiguationData":[TD([[makeQuery(id+"F0.imprint","IMPRINT",EDGE,{"disambiguationData":[TD([[subQ2,-1.0]])],"derivedFrom":subQ1}),-1.0]])]});}
            var Q26;
            {var subQ0=sQuery(id+"F0.wireOp",EDGE,"E66");var subQ1=sQuery(id+"F0.wireOp",EDGE,"E33");var subQ2=makeQuery(id+"F0.imprint","INTERSECT",VERTEX,{"derivedFrom":[subQ1,subQ0]});Q26=makeQuery(id+"F0.imprint","IMPRINT",FACE,{"disambiguationData":[TD([[makeQuery(id+"F0.imprint","IMPRINT",EDGE,{"disambiguationData":[TD([[subQ2,1.0]])],"derivedFrom":subQ1}),-1.0]])]});}
            var Q27;
            {var subQ4=sQuery(id+"F0.wireOp",EDGE,"E62.MirrorCS");var subQ5=sQuery(id+"F0.wireOp",EDGE,"E33");var subQ6=makeQuery(id+"F0.imprint","INTERSECT",VERTEX,{"derivedFrom":[subQ5,subQ4]});Q27=makeQuery(id+"F0.imprint","IMPRINT",FACE,{"disambiguationData":[TD([[makeQuery(id+"F0.imprint","IMPRINT",EDGE,{"disambiguationData":[TD([[subQ6,-1.0]])],"derivedFrom":subQ5}),-1.0]])]});}
            extrude(context, id + "F8", {"entities" : qUnion([Q0, Q1, Q2, Q3, Q4, Q5, Q6, Q7, Q8, Q9, Q10, Q11, Q12, Q13, Q14, Q15, Q16, Q17, Q18, Q19, Q20, Q21, Q22, Q23, Q24, Q25, Q26, Q27]), "operationType" : NewBodyOperationType.ADD, "depth" : 5 * mm, "offsetDistance" : 25 * mm, "hasSecondDirection" : true, "secondDirectionOppositeDirection" : true, "secondDirectionDepth" : 5 * mm});
        }
        {
            var Q0;
            {var subQ0=sQuery(id+"F0.wireOp",EDGE,"E32");var subQ1=sQuery(id+"F0.wireOp",EDGE,"E33");Q0=makeQuery(id+"F7.boolean.opBoolean","MERGE",FACE,{"derivedFrom":[makeQuery(id+"F5.boolean.opBoolean","MERGE",FACE,{"derivedFrom":[makeQuery(id+"F1.opExtrude","CAP_FACE",FACE,{"disambiguationData":[OSD([sQuery(id+"F0.wireOp",EDGE,"E4"),sQuery(id+"F0.wireOp",EDGE,"E6.MirrorCS"),sQuery(id+"F0.wireOp",EDGE,"E7"),sQuery(id+"F0.wireOp",EDGE,"E9"),sQuery(id+"F0.wireOp",EDGE,"E10.1.1"),sQuery(id+"F0.wireOp",EDGE,"E10.1.2"),sQuery(id+"F0.wireOp",EDGE,"E10.1.3"),sQuery(id+"F0.wireOp",EDGE,"E10.1.4"),sQuery(id+"F0.wireOp",EDGE,"E10.2.1"),sQuery(id+"F0.wireOp",EDGE,"E10.2.2"),sQuery(id+"F0.wireOp",EDGE,"E10.2.3"),sQuery(id+"F0.wireOp",EDGE,"E10.2.4"),sQuery(id+"F0.wireOp",EDGE,"E10.3.1"),sQuery(id+"F0.wireOp",EDGE,"E10.3.2"),sQuery(id+"F0.wireOp",EDGE,"E10.3.3"),sQuery(id+"F0.wireOp",EDGE,"E10.3.4"),sQuery(id+"F0.wireOp",EDGE,"E10.4.1"),sQuery(id+"F0.wireOp",EDGE,"E10.4.2"),sQuery(id+"F0.wireOp",EDGE,"E10.4.3"),sQuery(id+"F0.wireOp",EDGE,"E10.4.4"),sQuery(id+"F0.wireOp",EDGE,"E10.5.1"),sQuery(id+"F0.wireOp",EDGE,"E10.5.2"),sQuery(id+"F0.wireOp",EDGE,"E10.5.3"),sQuery(id+"F0.wireOp",EDGE,"E10.5.4"),sQuery(id+"F0.wireOp",EDGE,"E10.6.1"),sQuery(id+"F0.wireOp",EDGE,"E10.6.2"),sQuery(id+"F0.wireOp",EDGE,"E10.6.3"),sQuery(id+"F0.wireOp",EDGE,"E10.6.4"),sQuery(id+"F0.wireOp",EDGE,"E10.7.1"),sQuery(id+"F0.wireOp",EDGE,"E10.7.2"),sQuery(id+"F0.wireOp",EDGE,"E10.7.3"),sQuery(id+"F0.wireOp",EDGE,"E10.7.4"),sQuery(id+"F0.wireOp",EDGE,"E10.8.1"),sQuery(id+"F0.wireOp",EDGE,"E10.8.2"),sQuery(id+"F0.wireOp",EDGE,"E10.8.3"),sQuery(id+"F0.wireOp",EDGE,"E10.8.4"),sQuery(id+"F0.wireOp",EDGE,"E10.9.1"),sQuery(id+"F0.wireOp",EDGE,"E10.9.2"),sQuery(id+"F0.wireOp",EDGE,"E10.9.3"),sQuery(id+"F0.wireOp",EDGE,"E10.9.4"),sQuery(id+"F0.wireOp",EDGE,"E10.10.1"),sQuery(id+"F0.wireOp",EDGE,"E10.10.2"),sQuery(id+"F0.wireOp",EDGE,"E10.10.3"),sQuery(id+"F0.wireOp",EDGE,"E10.10.4"),sQuery(id+"F0.wireOp",EDGE,"E10.11.1"),sQuery(id+"F0.wireOp",EDGE,"E10.11.2"),sQuery(id+"F0.wireOp",EDGE,"E10.11.3"),sQuery(id+"F0.wireOp",EDGE,"E10.11.4"),sQuery(id+"F0.wireOp",EDGE,"E10.12.1"),sQuery(id+"F0.wireOp",EDGE,"E10.12.2"),sQuery(id+"F0.wireOp",EDGE,"E10.12.3"),sQuery(id+"F0.wireOp",EDGE,"E10.12.4"),sQuery(id+"F0.wireOp",EDGE,"E10.13.1"),sQuery(id+"F0.wireOp",EDGE,"E10.13.2"),sQuery(id+"F0.wireOp",EDGE,"E10.13.3"),sQuery(id+"F0.wireOp",EDGE,"E10.13.4"),sQuery(id+"F0.wireOp",EDGE,"E10.14.1"),sQuery(id+"F0.wireOp",EDGE,"E10.14.2"),sQuery(id+"F0.wireOp",EDGE,"E10.14.3"),sQuery(id+"F0.wireOp",EDGE,"E10.14.4"),sQuery(id+"F0.wireOp",EDGE,"E10.15.1"),sQuery(id+"F0.wireOp",EDGE,"E10.15.2"),sQuery(id+"F0.wireOp",EDGE,"E10.15.3"),sQuery(id+"F0.wireOp",EDGE,"E10.15.4"),sQuery(id+"F0.wireOp",EDGE,"E10.16.1"),sQuery(id+"F0.wireOp",EDGE,"E10.16.2"),sQuery(id+"F0.wireOp",EDGE,"E10.16.3"),sQuery(id+"F0.wireOp",EDGE,"E10.16.4"),sQuery(id+"F0.wireOp",EDGE,"E10.17.1"),sQuery(id+"F0.wireOp",EDGE,"E10.17.2"),sQuery(id+"F0.wireOp",EDGE,"E10.17.3"),sQuery(id+"F0.wireOp",EDGE,"E10.17.4"),sQuery(id+"F0.wireOp",EDGE,"E10.18.1"),sQuery(id+"F0.wireOp",EDGE,"E10.18.2"),sQuery(id+"F0.wireOp",EDGE,"E10.18.3"),sQuery(id+"F0.wireOp",EDGE,"E10.18.4"),sQuery(id+"F0.wireOp",EDGE,"E10.19.1"),sQuery(id+"F0.wireOp",EDGE,"E10.19.2"),sQuery(id+"F0.wireOp",EDGE,"E10.19.3"),sQuery(id+"F0.wireOp",EDGE,"E10.19.4"),sQuery(id+"F0.wireOp",EDGE,"E10.20.1"),sQuery(id+"F0.wireOp",EDGE,"E10.20.2"),sQuery(id+"F0.wireOp",EDGE,"E10.20.3"),sQuery(id+"F0.wireOp",EDGE,"E10.20.4"),sQuery(id+"F0.wireOp",EDGE,"E10.21.1"),sQuery(id+"F0.wireOp",EDGE,"E10.21.2"),sQuery(id+"F0.wireOp",EDGE,"E10.21.3"),sQuery(id+"F0.wireOp",EDGE,"E10.21.4"),sQuery(id+"F0.wireOp",EDGE,"E10.22.1"),sQuery(id+"F0.wireOp",EDGE,"E10.22.2"),sQuery(id+"F0.wireOp",EDGE,"E10.22.3"),sQuery(id+"F0.wireOp",EDGE,"E10.22.4"),sQuery(id+"F0.wireOp",EDGE,"E10.23.0"),sQuery(id+"F0.wireOp",EDGE,"E10.23.1"),sQuery(id+"F0.wireOp",EDGE,"E10.23.2"),sQuery(id+"F0.wireOp",EDGE,"E10.23.3"),sQuery(id+"F0.wireOp",EDGE,"E10.23.4"),sQuery(id+"F0.wireOp",EDGE,"E21.bottom"),sQuery(id+"F0.wireOp",EDGE,"E21.top"),sQuery(id+"F0.wireOp",EDGE,"E21.left"),sQuery(id+"F0.wireOp",EDGE,"E21.right"),sQuery(id+"F0.wireOp",EDGE,"E22.bottom"),sQuery(id+"F0.wireOp",EDGE,"E22.top"),sQuery(id+"F0.wireOp",EDGE,"E22.left"),sQuery(id+"F0.wireOp",EDGE,"E22.right"),sQuery(id+"F0.wireOp",EDGE,"E23.MirrorCS"),sQuery(id+"F0.wireOp",EDGE,"E24.MirrorCS"),sQuery(id+"F0.wireOp",EDGE,"E25.MirrorCS"),sQuery(id+"F0.wireOp",EDGE,"E26.MirrorCS"),sQuery(id+"F0.wireOp",EDGE,"E27.MirrorCS"),sQuery(id+"F0.wireOp",EDGE,"E28.MirrorCS"),sQuery(id+"F0.wireOp",EDGE,"E29.MirrorCS"),sQuery(id+"F0.wireOp",EDGE,"E30.MirrorCS"),subQ1,sQuery(id+"F0.wireOp",EDGE,"E33"),sQuery(id+"F0.wireOp",EDGE,"E37"),sQuery(id+"F0.wireOp",EDGE,"E38"),sQuery(id+"F0.wireOp",EDGE,"E40"),sQuery(id+"F0.wireOp",EDGE,"E41.MirrorCS"),sQuery(id+"F0.wireOp",EDGE,"E42.MirrorCS"),sQuery(id+"F0.wireOp",EDGE,"E43.MirrorCS"),sQuery(id+"F0.wireOp",EDGE,"E44.MirrorCS"),sQuery(id+"F0.wireOp",EDGE,"E45.MirrorCS"),sQuery(id+"F0.wireOp",EDGE,"E46.MirrorCS"),sQuery(id+"F0.wireOp",EDGE,"E47.MirrorCS"),sQuery(id+"F0.wireOp",EDGE,"E48.MirrorCS"),sQuery(id+"F0.wireOp",EDGE,"E49.MirrorCS")])],"isStart":false}),makeQuery(id+"F5.opExtrude","CAP_FACE",FACE,{"disambiguationData":[OSD([subQ0,subQ1])],"isStart":true})]}),makeQuery(id+"F7.opExtrude","CAP_FACE",FACE,{"disambiguationData":[OSD([subQ0])],"isStart":false})]});}
            var sketch = newSketch(context, id + "F9", { "sketchPlane" : qUnion([Q0])});
            skText(sketch, "E108", { "text": "ClusterBot", "fontName": "OpenSans-Bold.ttf"});
            skPoint(sketch, "E109.endSnap0", {"position": v(-65, 0) * mm});
            const initialGuessF9  = {"E108": [-0.04602, -0.0025, 1, 0, 0.005]};
            skSetInitialGuess(sketch, initialGuessF9);
            skSolve(sketch);
        }
        {
            var Q0;
            Q0 = qSketchRegion(id + "F9", true);
            extrude(context, id + "F10", {"entities" : qUnion([Q0]), "operationType" : NewBodyOperationType.ADD, "depth" : 2 * mm, "offsetDistance" : 25 * mm});
        }
    });
